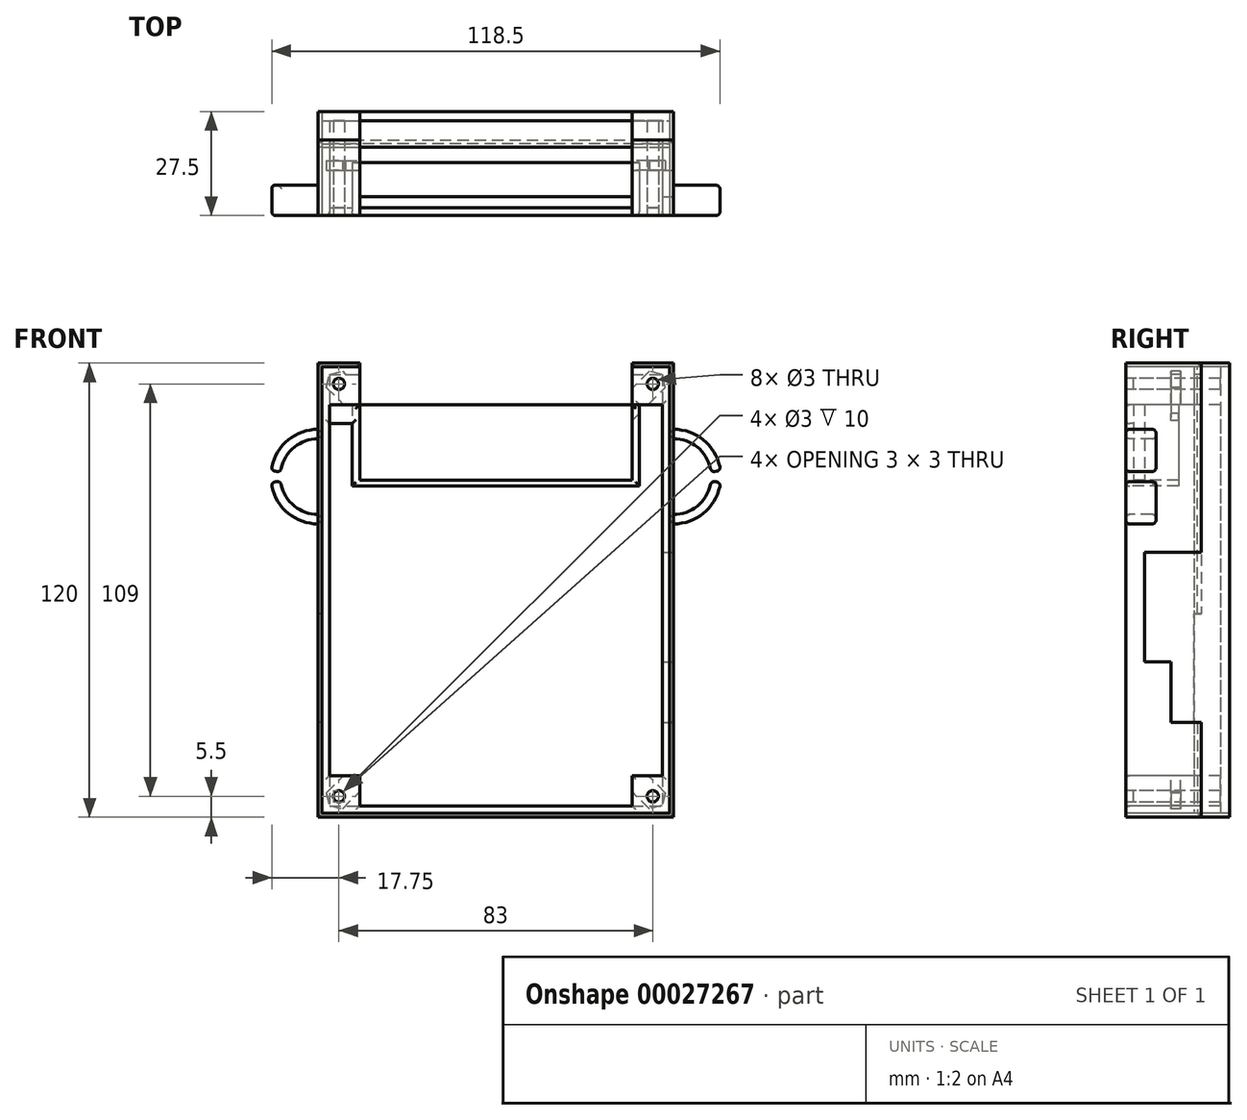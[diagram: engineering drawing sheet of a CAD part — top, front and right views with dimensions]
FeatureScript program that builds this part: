
annotation { "Feature Type Name" : "Feature", "Feature Type Description" : "" }
export const myFeature = defineFeature(function(context is Context, id is Id, definition is map)
    precondition{}
    {
        {
            var Q0;
            Q0=qCreatedBy(makeId("Front.planeOp"),FACE);
            var sketch = newSketch(context, id + "F0", { "sketchPlane" : qUnion([Q0])});
            skLineSegment(sketch, "E0.bottom", {"start": v(-41.5, 54.5) * mm, "end": v(41.5, 54.5) * mm, "construction": true});
            skLineSegment(sketch, "E1.left", {"start": v(-47, 60) * mm, "end": v(-47, -60) * mm});
            skLineSegment(sketch, "E0.top", {"start": v(-41.5, -54.5) * mm, "end": v(41.5, -54.5) * mm, "construction": true});
            skLineSegment(sketch, "E2.top", {"start": v(-46, -59) * mm, "end": v(46, -59) * mm});
            skLineSegment(sketch, "E0.left", {"start": v(-41.5, 54.5) * mm, "end": v(-41.5, -54.5) * mm, "construction": true});
            skLineSegment(sketch, "E2.left", {"start": v(-46, 59) * mm, "end": v(-46, -59) * mm});
            skLineSegment(sketch, "E2.right", {"start": v(46, 59) * mm, "end": v(46, -59) * mm});
            skLineSegment(sketch, "E3.left", {"start": v(-44, 57) * mm, "end": v(-44, -57) * mm});
            skLineSegment(sketch, "E0.right", {"start": v(41.5, 54.5) * mm, "end": v(41.5, -54.5) * mm, "construction": true});
            skLineSegment(sketch, "E2.bottom", {"start": v(-46, 59) * mm, "end": v(46, 59) * mm});
            skLineSegment(sketch, "E4", {"start": v(0, 57) * mm, "end": v(0, -57) * mm, "construction": true});
            skLineSegment(sketch, "E3.top", {"start": v(-44, -57) * mm, "end": v(44, -57) * mm});
            skLineSegment(sketch, "E5.right", {"start": v(36, -57) * mm, "end": v(36, -49) * mm});
            skLineSegment(sketch, "E6", {"start": v(-46, 0) * mm, "end": v(46, 0) * mm, "construction": true});
            skLineSegment(sketch, "E1.right", {"start": v(47, 60) * mm, "end": v(47, -60) * mm});
            skLineSegment(sketch, "E7.top", {"start": v(-44, -49) * mm, "end": v(-36, -49) * mm});
            skLineSegment(sketch, "E8.top", {"start": v(-44, 49) * mm, "end": v(-36, 49) * mm});
            skLineSegment(sketch, "E9.right", {"start": v(36, 57) * mm, "end": v(36, 49) * mm});
            skLineSegment(sketch, "E1.top", {"start": v(-47, -60) * mm, "end": v(47, -60) * mm});
            skLineSegment(sketch, "E7.right", {"start": v(-36, -57) * mm, "end": v(-36, -49) * mm});
            skLineSegment(sketch, "E5.top", {"start": v(44, -49) * mm, "end": v(36, -49) * mm});
            skLineSegment(sketch, "E3.right", {"start": v(44, 57) * mm, "end": v(44, -57) * mm});
            skPoint(sketch, "E10.rect.middle", {"position": v(0, 0) * mm});
            skLineSegment(sketch, "E8.right", {"start": v(-36, 57) * mm, "end": v(-36, 49) * mm});
            skLineSegment(sketch, "E3.bottom", {"start": v(-44, 57) * mm, "end": v(44, 57) * mm});
            skLineSegment(sketch, "E1.bottom", {"start": v(-47, 60) * mm, "end": v(47, 60) * mm});
            skLineSegment(sketch, "E9.top", {"start": v(44, 49) * mm, "end": v(36, 49) * mm});
            skLineSegment(sketch, "E7.bottom", {"start": v(-44, -57) * mm, "end": v(-36, -57) * mm});
            skLineSegment(sketch, "E7.left", {"start": v(-44, -57) * mm, "end": v(-44, -49) * mm});
            skLineSegment(sketch, "E11", {"start": v(0, 60) * mm, "end": v(0, -60) * mm, "construction": true});
            skLineSegment(sketch, "E12", {"start": v(0, 59) * mm, "end": v(0, -59) * mm, "construction": true});
            skLineSegment(sketch, "E5.bottom", {"start": v(44, -57) * mm, "end": v(36, -57) * mm});
            skLineSegment(sketch, "E13", {"start": v(-47, 0) * mm, "end": v(47, 0) * mm, "construction": true});
            skLineSegment(sketch, "E8.left", {"start": v(-44, 57) * mm, "end": v(-44, 49) * mm});
            skLineSegment(sketch, "E8.bottom", {"start": v(-44, 57) * mm, "end": v(-36, 57) * mm});
            skLineSegment(sketch, "E9.left", {"start": v(44, 57) * mm, "end": v(44, 49) * mm});
            skLineSegment(sketch, "E14", {"start": v(0, 54.5) * mm, "end": v(0, -54.5) * mm, "construction": true});
            skLineSegment(sketch, "E5.left", {"start": v(44, -57) * mm, "end": v(44, -49) * mm});
            skLineSegment(sketch, "E15", {"start": v(-44, 0) * mm, "end": v(44, 0) * mm, "construction": true});
            skLineSegment(sketch, "E9.bottom", {"start": v(44, 57) * mm, "end": v(36, 57) * mm});
            skLineSegment(sketch, "E16", {"start": v(-41.5, 0) * mm, "end": v(41.5, 0) * mm, "construction": true});
            skCircle(sketch, "E17", {"center": v(41.5, 54.5) * mm, "radius": 1.5 * mm});
            skCircle(sketch, "E18", {"center": v(-41.5, -54.5) * mm, "radius": 1.5 * mm});
            skCircle(sketch, "E19", {"center": v(41.5, -54.5) * mm, "radius": 1.5 * mm});
            skCircle(sketch, "E20", {"center": v(-41.5, 54.5) * mm, "radius": 1.5 * mm});
            skLineSegment(sketch, "E21.bottom", {"start": v(36, 60) * mm, "end": v(-36, 60) * mm});
            skLineSegment(sketch, "E21.top", {"start": v(36, 49) * mm, "end": v(-36, 49) * mm});
            skLineSegment(sketch, "E21.left", {"start": v(36, 60) * mm, "end": v(36, 49) * mm});
            skLineSegment(sketch, "E21.right", {"start": v(-36, 60) * mm, "end": v(-36, 49) * mm});
            skLineSegment(sketch, "E22.top", {"start": v(36, 29) * mm, "end": v(-36, 29) * mm});
            skLineSegment(sketch, "E22.left", {"start": v(36, 49) * mm, "end": v(36, 29) * mm});
            skLineSegment(sketch, "E22.right", {"start": v(-36, 49) * mm, "end": v(-36, 29) * mm});
            skLineSegment(sketch, "E23.bottom", {"start": v(38, 49) * mm, "end": v(-38, 49) * mm});
            skLineSegment(sketch, "E23.top", {"start": v(38, 27.5) * mm, "end": v(-38, 27.5) * mm});
            skLineSegment(sketch, "E23.left", {"start": v(38, 49) * mm, "end": v(38, 27.5) * mm});
            skLineSegment(sketch, "E23.right", {"start": v(-38, 49) * mm, "end": v(-38, 27.5) * mm});
            skLineSegment(sketch, "E24.bottom", {"start": v(-44, 49) * mm, "end": v(-38, 49) * mm});
            skLineSegment(sketch, "E24.top", {"start": v(-44, 44) * mm, "end": v(-38, 44) * mm});
            skLineSegment(sketch, "E24.left", {"start": v(-44, 49) * mm, "end": v(-44, 44) * mm});
            skLineSegment(sketch, "E24.right", {"start": v(-38, 49) * mm, "end": v(-38, 44) * mm});
            skLineSegment(sketch, "E25.bottom", {"start": v(44, 49) * mm, "end": v(38, 49) * mm});
            skLineSegment(sketch, "E25.top", {"start": v(44, 44) * mm, "end": v(38, 44) * mm});
            skLineSegment(sketch, "E25.left", {"start": v(44, 49) * mm, "end": v(44, 44) * mm});
            skLineSegment(sketch, "E25.right", {"start": v(38, 49) * mm, "end": v(38, 44) * mm});
            skSolve(sketch);
        }
        {
            var Q0;
            Q0=makeQuery(id+"F0.imprint","IMPRINT",FACE,{"disambiguationData":[TD([[makeQuery(id+"F0.imprint","IMPRINT",EDGE,{"derivedFrom":sQuery(id+"F0.wireOp",EDGE,"E3.left")}),1.0]])]});
            var Q1;
            Q1=makeQuery(id+"F0.imprint","IMPRINT",FACE,{"disambiguationData":[TD([[makeQuery(id+"F0.imprint","IMPRINT",EDGE,{"derivedFrom":sQuery(id+"F0.wireOp",EDGE,"E2.top")}),1.0]])]});
            var Q2;
            {var subQ1=sQuery(id+"F0.wireOp",EDGE,"E9.top");Q2=makeQuery(id+"F0.imprint","IMPRINT",FACE,{"disambiguationData":[TD([[makeQuery(id+"F0.imprint","IMPRINT",EDGE,{"derivedFrom":subQ1}),-1.0]])]});}
            var Q3;
            Q3=makeQuery(id+"F0.imprint","IMPRINT",FACE,{"disambiguationData":[TD([[makeQuery(id+"F0.imprint","IMPRINT",EDGE,{"derivedFrom":sQuery(id+"F0.wireOp",EDGE,"E5.right")}),-1.0]])]});
            var Q4;
            Q4=makeQuery(id+"F0.imprint","IMPRINT",FACE,{"disambiguationData":[TD([[makeQuery(id+"F0.imprint","IMPRINT",EDGE,{"derivedFrom":sQuery(id+"F0.wireOp",EDGE,"E21.top")}),1.0]])]});
            var Q5;
            {var subQ8=sQuery(id+"F0.wireOp",EDGE,"E1.left");Q5=makeQuery(id+"F0.imprint","IMPRINT",FACE,{"disambiguationData":[TD([[makeQuery(id+"F0.imprint","IMPRINT",EDGE,{"derivedFrom":subQ8}),1.0]])]});}
            var Q6;
            Q6=makeQuery(id+"F0.imprint","IMPRINT",FACE,{"disambiguationData":[TD([[makeQuery(id+"F0.imprint","IMPRINT",EDGE,{"derivedFrom":sQuery(id+"F0.wireOp",EDGE,"E7.top")}),-1.0]])]});
            var Q7;
            Q7=makeQuery(id+"F0.imprint","IMPRINT",FACE,{"disambiguationData":[TD([[makeQuery(id+"F0.imprint","IMPRINT",EDGE,{"derivedFrom":sQuery(id+"F0.wireOp",EDGE,"E17")}),1.0]])]});
            var Q8;
            {var subQ0=sQuery(id+"F0.wireOp",EDGE,"E8.top");Q8=makeQuery(id+"F0.imprint","IMPRINT",FACE,{"disambiguationData":[TD([[makeQuery(id+"F0.imprint","IMPRINT",EDGE,{"derivedFrom":subQ0}),1.0]])]});}
            var Q9;
            Q9=makeQuery(id+"F0.imprint","IMPRINT",FACE,{"disambiguationData":[TD([[makeQuery(id+"F0.imprint","IMPRINT",EDGE,{"derivedFrom":sQuery(id+"F0.wireOp",EDGE,"E19")}),1.0]])]});
            var Q10;
            Q10=makeQuery(id+"F0.imprint","IMPRINT",FACE,{"disambiguationData":[TD([[makeQuery(id+"F0.imprint","IMPRINT",EDGE,{"derivedFrom":sQuery(id+"F0.wireOp",EDGE,"E20")}),1.0]])]});
            var Q11;
            Q11=makeQuery(id+"F0.imprint","IMPRINT",FACE,{"disambiguationData":[TD([[makeQuery(id+"F0.imprint","IMPRINT",EDGE,{"derivedFrom":sQuery(id+"F0.wireOp",EDGE,"E18")}),1.0]])]});
            var Q12;
            Q12=makeQuery(id+"F0.imprint","IMPRINT",FACE,{"disambiguationData":[TD([[makeQuery(id+"F0.imprint","IMPRINT",EDGE,{"derivedFrom":sQuery(id+"F0.wireOp",EDGE,"E22.top")}),1.0]])]});
            var Q13;
            Q13=makeQuery(id+"F0.imprint","IMPRINT",FACE,{"disambiguationData":[TD([[makeQuery(id+"F0.imprint","IMPRINT",EDGE,{"derivedFrom":sQuery(id+"F0.wireOp",EDGE,"E25.bottom")}),1.0]])]});
            var Q14;
            Q14=makeQuery(id+"F0.imprint","IMPRINT",FACE,{"disambiguationData":[TD([[makeQuery(id+"F0.imprint","IMPRINT",EDGE,{"derivedFrom":sQuery(id+"F0.wireOp",EDGE,"E24.bottom")}),-1.0]])]});
            var Q15;
            Q15=makeQuery(id+"F0.imprint","IMPRINT",FACE,{"disambiguationData":[TD([[makeQuery(id+"F0.imprint","IMPRINT",EDGE,{"derivedFrom":sQuery(id+"F0.wireOp",EDGE,"E8.left")}),1.0]])]});
            var Q16;
            Q16=makeQuery(id+"F0.imprint","IMPRINT",FACE,{"disambiguationData":[TD([[makeQuery(id+"F0.imprint","IMPRINT",EDGE,{"derivedFrom":sQuery(id+"F0.wireOp",EDGE,"E9.left")}),-1.0]])]});
            extrude(context, id + "F1", {"entities" : qUnion([Q0, Q1, Q2, Q3, Q4, Q5, Q6, Q7, Q8, Q9, Q10, Q11, Q12, Q13, Q14, Q15, Q16]), "oppositeDirection" : true, "depth" : 2 * mm});
        }
        {
            var Q0;
            Q0=makeQuery(id+"F0.imprint","IMPRINT",FACE,{"disambiguationData":[TD([[makeQuery(id+"F0.imprint","IMPRINT",EDGE,{"derivedFrom":sQuery(id+"F0.wireOp",EDGE,"E2.top")}),1.0]])]});
            extrude(context, id + "F2", {"entities" : qUnion([Q0]), "operationType" : NewBodyOperationType.ADD, "oppositeDirection" : true, "depth" : 18 * mm});
        }
        {
            var Q0;
            {var subQ8=sQuery(id+"F0.wireOp",EDGE,"E1.left");Q0=makeQuery(id+"F0.imprint","IMPRINT",FACE,{"disambiguationData":[TD([[makeQuery(id+"F0.imprint","IMPRINT",EDGE,{"derivedFrom":subQ8}),1.0]])]});}
            var Q1;
            Q1=makeQuery(id+"F0.imprint","IMPRINT",FACE,{"disambiguationData":[TD([[makeQuery(id+"F0.imprint","IMPRINT",EDGE,{"derivedFrom":sQuery(id+"F0.wireOp",EDGE,"E7.top")}),-1.0]])]});
            var Q2;
            {var subQ0=sQuery(id+"F0.wireOp",EDGE,"E8.top");Q2=makeQuery(id+"F0.imprint","IMPRINT",FACE,{"disambiguationData":[TD([[makeQuery(id+"F0.imprint","IMPRINT",EDGE,{"derivedFrom":subQ0}),1.0]])]});}
            var Q3;
            {var subQ1=sQuery(id+"F0.wireOp",EDGE,"E9.top");Q3=makeQuery(id+"F0.imprint","IMPRINT",FACE,{"disambiguationData":[TD([[makeQuery(id+"F0.imprint","IMPRINT",EDGE,{"derivedFrom":subQ1}),-1.0]])]});}
            var Q4;
            Q4=makeQuery(id+"F0.imprint","IMPRINT",FACE,{"disambiguationData":[TD([[makeQuery(id+"F0.imprint","IMPRINT",EDGE,{"derivedFrom":sQuery(id+"F0.wireOp",EDGE,"E8.left")}),1.0]])]});
            var Q5;
            Q5=makeQuery(id+"F0.imprint","IMPRINT",FACE,{"disambiguationData":[TD([[makeQuery(id+"F0.imprint","IMPRINT",EDGE,{"derivedFrom":sQuery(id+"F0.wireOp",EDGE,"E24.bottom")}),-1.0]])]});
            var Q6;
            Q6=makeQuery(id+"F0.imprint","IMPRINT",FACE,{"disambiguationData":[TD([[makeQuery(id+"F0.imprint","IMPRINT",EDGE,{"derivedFrom":sQuery(id+"F0.wireOp",EDGE,"E9.left")}),-1.0]])]});
            var Q7;
            Q7=makeQuery(id+"F0.imprint","IMPRINT",FACE,{"disambiguationData":[TD([[makeQuery(id+"F0.imprint","IMPRINT",EDGE,{"derivedFrom":sQuery(id+"F0.wireOp",EDGE,"E5.right")}),-1.0]])]});
            var Q8;
            Q8=makeQuery(id+"F0.imprint","IMPRINT",FACE,{"disambiguationData":[TD([[makeQuery(id+"F0.imprint","IMPRINT",EDGE,{"derivedFrom":sQuery(id+"F0.wireOp",EDGE,"E25.bottom")}),1.0]])]});
            extrude(context, id + "F3", {"entities" : qUnion([Q0, Q1, Q2, Q3, Q4, Q5, Q6, Q7, Q8]), "operationType" : NewBodyOperationType.ADD, "oppositeDirection" : true, "depth" : 20 * mm});
        }
        {
            var Q0;
            Q0=makeQuery(id+"F0.imprint","IMPRINT",FACE,{"disambiguationData":[TD([[makeQuery(id+"F0.imprint","IMPRINT",EDGE,{"derivedFrom":sQuery(id+"F0.wireOp",EDGE,"E22.top")}),1.0]])]});
            extrude(context, id + "F4", {"entities" : qUnion([Q0]), "operationType" : NewBodyOperationType.ADD, "oppositeDirection" : true, "depth" : 14 * mm});
        }
        {
            var Q0;
            {var subQ0=sQuery(id+"F0.wireOp",EDGE,"E1.left");Q0=makeQuery(id+"F3.boolean.opBoolean","MERGE",FACE,{"derivedFrom":[makeQuery(id+"F1.opExtrude","SWEPT_FACE",FACE,{"disambiguationData":[OSD([subQ0])]}),makeQuery(id+"F3.opExtrude","SWEPT_FACE",FACE,{"disambiguationData":[OSD([subQ0])]})]});}
            var sketch = newSketch(context, id + "F5", { "sketchPlane" : qUnion([Q0])});
            skLineSegment(sketch, "E26.bottom", {"start": v(-20, -35) * mm, "end": v(-18, -35) * mm});
            skLineSegment(sketch, "E26.top", {"start": v(-20, -6.2) * mm, "end": v(-18, -6.2) * mm});
            skLineSegment(sketch, "E26.left", {"start": v(-20, -35) * mm, "end": v(-20, -6.2) * mm});
            skLineSegment(sketch, "E26.right", {"start": v(-18, -35) * mm, "end": v(-18, -6.2) * mm});
            skSolve(sketch);
        }
        {
            var Q0;
            {var subQ0=sQuery(id+"F0.wireOp",EDGE,"E1.right");Q0=makeQuery(id+"F3.boolean.opBoolean","MERGE",FACE,{"derivedFrom":[makeQuery(id+"F1.opExtrude","SWEPT_FACE",FACE,{"disambiguationData":[OSD([subQ0])]}),makeQuery(id+"F3.opExtrude","SWEPT_FACE",FACE,{"disambiguationData":[OSD([subQ0])]})]});}
            var sketch = newSketch(context, id + "F6", { "sketchPlane" : qUnion([Q0])});
            skLineSegment(sketch, "E27.bottom", {"start": v(20, -35) * mm, "end": v(12, -35) * mm});
            skLineSegment(sketch, "E27.top", {"start": v(20, -19) * mm, "end": v(12, -19) * mm});
            skLineSegment(sketch, "E27.left", {"start": v(20, -35) * mm, "end": v(20, -19) * mm});
            skLineSegment(sketch, "E27.right", {"start": v(12, -35) * mm, "end": v(12, -19) * mm});
            skLineSegment(sketch, "E28.bottom", {"start": v(20, -19) * mm, "end": v(5, -19) * mm});
            skLineSegment(sketch, "E28.top", {"start": v(20, 10) * mm, "end": v(5, 10) * mm});
            skLineSegment(sketch, "E28.left", {"start": v(20, -19) * mm, "end": v(20, 10) * mm});
            skLineSegment(sketch, "E28.right", {"start": v(5, -19) * mm, "end": v(5, 10) * mm});
            skSolve(sketch);
        }
        {
            var Q0;
            Q0=makeQuery(id+"F5.imprint","IMPRINT",FACE,{"disambiguationData":[TD([[makeQuery(id+"F5.imprint","IMPRINT",EDGE,{"derivedFrom":sQuery(id+"F5.wireOp",EDGE,"E26.bottom")}),1.0]])]});
            extrude(context, id + "F7", {"entities" : qUnion([Q0]), "operationType" : NewBodyOperationType.REMOVE, "endBound" : BoundingType.UP_TO_NEXT, "oppositeDirection" : true, "depth" : 25 * mm});
        }
        {
            var Q0;
            Q0=makeQuery(id+"F6.imprint","IMPRINT",FACE,{"disambiguationData":[TD([[makeQuery(id+"F6.imprint","IMPRINT",EDGE,{"derivedFrom":sQuery(id+"F6.wireOp",EDGE,"E27.bottom")}),-1.0]])]});
            var Q1;
            Q1=makeQuery(id+"F6.imprint","IMPRINT",FACE,{"disambiguationData":[TD([[makeQuery(id+"F6.imprint","IMPRINT",EDGE,{"derivedFrom":sQuery(id+"F6.wireOp",EDGE,"E28.top")}),1.0]])]});
            extrude(context, id + "F8", {"entities" : qUnion([Q0, Q1]), "operationType" : NewBodyOperationType.REMOVE, "endBound" : BoundingType.UP_TO_NEXT, "oppositeDirection" : true, "depth" : 25 * mm});
        }
        {
            var Q0;
            Q0=makeQuery(id+"F8.boolean.opBoolean","COPY",FACE,{"derivedFrom":makeQuery(id+"F8.opExtrude","SWEPT_FACE",FACE,{"disambiguationData":[OSD([sQuery(id+"F6.wireOp",EDGE,"E27.right")])]})});
            var sketch = newSketch(context, id + "F9", { "sketchPlane" : qUnion([Q0])});
            skLineSegment(sketch, "E29.0", {"start": v(-36, -57) * mm, "end": v(-36, -49) * mm});
            skCircle(sketch, "E29.1", {"center": v(-41.5, -54.5) * mm, "radius": 1.5 * mm});
            skLineSegment(sketch, "E29.2", {"start": v(-44, -57) * mm, "end": v(-36, -57) * mm});
            skLineSegment(sketch, "E29.3", {"start": v(-44, -57) * mm, "end": v(-44, -49) * mm});
            skLineSegment(sketch, "E29.4", {"start": v(-44, -49) * mm, "end": v(-36, -49) * mm});
            skLineSegment(sketch, "E30", {"start": v(-42.4, -51.15) * mm, "end": v(-44.85, -53.6) * mm});
            skLineSegment(sketch, "E31", {"start": v(-44.85, -53.6) * mm, "end": v(-43.95, -56.95) * mm});
            skLineSegment(sketch, "E32", {"start": v(-43.95, -56.95) * mm, "end": v(-40.6, -57.85) * mm});
            skLineSegment(sketch, "E33", {"start": v(-40.6, -57.85) * mm, "end": v(-38.15, -55.4) * mm});
            skLineSegment(sketch, "E34", {"start": v(-38.15, -55.4) * mm, "end": v(-39.05, -52.05) * mm});
            skLineSegment(sketch, "E35", {"start": v(-39.05, -52.05) * mm, "end": v(-42.4, -51.15) * mm});
            skLineSegment(sketch, "E36", {"start": v(-42.4, -51.15) * mm, "end": v(-40.6, -57.85) * mm, "construction": true});
            skLineSegment(sketch, "E37", {"start": v(-44.85, -53.6) * mm, "end": v(-38.15, -55.4) * mm, "construction": true});
            skLineSegment(sketch, "E38", {"start": v(-43.95, -56.95) * mm, "end": v(-39.05, -52.05) * mm, "construction": true});
            skLineSegment(sketch, "E39", {"start": v(-44, -57) * mm, "end": v(-36, -49) * mm, "construction": true});
            skLineSegment(sketch, "E40", {"start": v(-38.15, -55.4) * mm, "end": v(-36, -53.24) * mm});
            skLineSegment(sketch, "E41", {"start": v(-36, -53.24) * mm, "end": v(-36, -49) * mm});
            skLineSegment(sketch, "E42", {"start": v(-42.4, -51.15) * mm, "end": v(-40.24, -49) * mm});
            skLineSegment(sketch, "E43", {"start": v(-40.24, -49) * mm, "end": v(-36, -49) * mm});
            skLineSegment(sketch, "E44.MirrorCS", {"start": v(40.24, -49) * mm, "end": v(36, -49) * mm});
            skLineSegment(sketch, "E45.MirrorCS", {"start": v(36, -53.24) * mm, "end": v(36, -49) * mm});
            skLineSegment(sketch, "E46.MirrorCS", {"start": v(43.95, -56.95) * mm, "end": v(39.05, -52.05) * mm});
            skLineSegment(sketch, "E47.MirrorCS", {"start": v(44.85, -53.6) * mm, "end": v(38.15, -55.4) * mm});
            skLineSegment(sketch, "E48.MirrorCS", {"start": v(42.4, -51.15) * mm, "end": v(40.6, -57.85) * mm});
            skLineSegment(sketch, "E49.MirrorCS", {"start": v(44, -57) * mm, "end": v(36, -49) * mm});
            skLineSegment(sketch, "E50.MirrorCS", {"start": v(43.95, -56.95) * mm, "end": v(40.6, -57.85) * mm});
            skPoint(sketch, "E51.MirrorP", {"position": v(41.5, -54.5) * mm});
            skLineSegment(sketch, "E52.MirrorCS", {"start": v(44, -57) * mm, "end": v(44, -49) * mm});
            skLineSegment(sketch, "E53.MirrorCS", {"start": v(39.05, -52.05) * mm, "end": v(42.4, -51.15) * mm});
            skLineSegment(sketch, "E54.MirrorCS", {"start": v(44, -49) * mm, "end": v(36, -49) * mm});
            skLineSegment(sketch, "E55.MirrorCS", {"start": v(42.4, -51.15) * mm, "end": v(40.24, -49) * mm});
            skLineSegment(sketch, "E56.MirrorCS", {"start": v(36, -57) * mm, "end": v(36, -49) * mm});
            skLineSegment(sketch, "E57.MirrorCS", {"start": v(40.6, -57.85) * mm, "end": v(38.15, -55.4) * mm});
            skLineSegment(sketch, "E58.MirrorCS", {"start": v(44, -57) * mm, "end": v(36, -57) * mm});
            skLineSegment(sketch, "E59.MirrorCS", {"start": v(38.15, -55.4) * mm, "end": v(36, -53.24) * mm});
            skCircle(sketch, "E60.MirrorC", {"center": v(41.5, -54.5) * mm, "radius": 1.5 * mm});
            skLineSegment(sketch, "E61.MirrorCS", {"start": v(38.15, -55.4) * mm, "end": v(39.05, -52.05) * mm});
            skLineSegment(sketch, "E62.MirrorCS", {"start": v(42.4, -51.15) * mm, "end": v(44.85, -53.6) * mm});
            skLineSegment(sketch, "E63.MirrorCS", {"start": v(44.85, -53.6) * mm, "end": v(43.95, -56.95) * mm});
            skLineSegment(sketch, "E64.MirrorCS", {"start": v(-43.95, 56.95) * mm, "end": v(-39.05, 52.05) * mm});
            skLineSegment(sketch, "E65.MirrorCS", {"start": v(-38.15, 55.4) * mm, "end": v(-36, 53.24) * mm});
            skLineSegment(sketch, "E66.MirrorCS", {"start": v(43.95, 56.95) * mm, "end": v(39.05, 52.05) * mm});
            skLineSegment(sketch, "E67.MirrorCS", {"start": v(40.24, 49) * mm, "end": v(36, 49) * mm});
            skLineSegment(sketch, "E68.MirrorCS", {"start": v(-38.15, 55.4) * mm, "end": v(-39.05, 52.05) * mm});
            skLineSegment(sketch, "E69.MirrorCS", {"start": v(36, 53.24) * mm, "end": v(36, 49) * mm});
            skLineSegment(sketch, "E70.MirrorCS", {"start": v(-36, 53.24) * mm, "end": v(-36, 49) * mm});
            skLineSegment(sketch, "E71.MirrorCS", {"start": v(-44, 57) * mm, "end": v(-36, 49) * mm});
            skLineSegment(sketch, "E72.MirrorCS", {"start": v(38.15, 55.4) * mm, "end": v(39.05, 52.05) * mm});
            skLineSegment(sketch, "E73.MirrorCS", {"start": v(-40.6, 57.85) * mm, "end": v(-38.15, 55.4) * mm});
            skLineSegment(sketch, "E74.MirrorCS", {"start": v(-39.05, 52.05) * mm, "end": v(-42.4, 51.15) * mm});
            skLineSegment(sketch, "E75.MirrorCS", {"start": v(-44.85, 53.6) * mm, "end": v(-38.15, 55.4) * mm});
            skLineSegment(sketch, "E76.MirrorCS", {"start": v(-42.4, 51.15) * mm, "end": v(-40.6, 57.85) * mm});
            skLineSegment(sketch, "E77.MirrorCS", {"start": v(-44.85, 53.6) * mm, "end": v(-43.95, 56.95) * mm});
            skLineSegment(sketch, "E78.MirrorCS", {"start": v(-42.4, 51.15) * mm, "end": v(-44.85, 53.6) * mm});
            skLineSegment(sketch, "E79.MirrorCS", {"start": v(43.95, 56.95) * mm, "end": v(40.6, 57.85) * mm});
            skLineSegment(sketch, "E80.MirrorCS", {"start": v(-44, 57) * mm, "end": v(-44, 49) * mm});
            skLineSegment(sketch, "E81.MirrorCS", {"start": v(38.15, 55.4) * mm, "end": v(36, 53.24) * mm});
            skLineSegment(sketch, "E82.MirrorCS", {"start": v(-43.95, 56.95) * mm, "end": v(-40.6, 57.85) * mm});
            skLineSegment(sketch, "E83.MirrorCS", {"start": v(40.6, 57.85) * mm, "end": v(38.15, 55.4) * mm});
            skLineSegment(sketch, "E84.MirrorCS", {"start": v(44, 57) * mm, "end": v(36, 49) * mm});
            skLineSegment(sketch, "E85.MirrorCS", {"start": v(42.4, 51.15) * mm, "end": v(44.85, 53.6) * mm});
            skLineSegment(sketch, "E86.MirrorCS", {"start": v(42.4, 51.15) * mm, "end": v(40.6, 57.85) * mm});
            skLineSegment(sketch, "E87.MirrorCS", {"start": v(42.4, 51.15) * mm, "end": v(40.24, 49) * mm});
            skLineSegment(sketch, "E88.MirrorCS", {"start": v(39.05, 52.05) * mm, "end": v(42.4, 51.15) * mm});
            skLineSegment(sketch, "E89.MirrorCS", {"start": v(44.85, 53.6) * mm, "end": v(43.95, 56.95) * mm});
            skCircle(sketch, "E90.MirrorC", {"center": v(-41.5, 54.5) * mm, "radius": 1.5 * mm});
            skLineSegment(sketch, "E91.MirrorCS", {"start": v(-36, 57) * mm, "end": v(-36, 49) * mm});
            skLineSegment(sketch, "E92.MirrorCS", {"start": v(44, 57) * mm, "end": v(36, 57) * mm});
            skLineSegment(sketch, "E93.MirrorCS", {"start": v(44.85, 53.6) * mm, "end": v(38.15, 55.4) * mm});
            skLineSegment(sketch, "E94.MirrorCS", {"start": v(-40.24, 49) * mm, "end": v(-36, 49) * mm});
            skCircle(sketch, "E95.MirrorC", {"center": v(41.5, 54.5) * mm, "radius": 1.5 * mm});
            skLineSegment(sketch, "E96.MirrorCS", {"start": v(-42.4, 51.15) * mm, "end": v(-40.24, 49) * mm});
            skLineSegment(sketch, "E97.MirrorCS", {"start": v(36, 57) * mm, "end": v(36, 49) * mm});
            skLineSegment(sketch, "E98.MirrorCS", {"start": v(44, 49) * mm, "end": v(36, 49) * mm});
            skLineSegment(sketch, "E99.MirrorCS", {"start": v(-44, 49) * mm, "end": v(-36, 49) * mm});
            skLineSegment(sketch, "E100.MirrorCS", {"start": v(44, 57) * mm, "end": v(44, 49) * mm});
            skLineSegment(sketch, "E101.MirrorCS", {"start": v(-44, 57) * mm, "end": v(-36, 57) * mm});
            skLineSegment(sketch, "E102.0", {"start": v(-36, 49) * mm, "end": v(-36, 29) * mm});
            skLineSegment(sketch, "E103.1", {"start": v(36, 49) * mm, "end": v(36, 29) * mm});
            skLineSegment(sketch, "E104", {"start": v(40.24, 49) * mm, "end": v(36, 44.76) * mm});
            skLineSegment(sketch, "E105", {"start": v(-40.24, 49) * mm, "end": v(-36, 44.76) * mm});
            skSolve(sketch);
        }
        {
            var Q0;
            {var subQ4=sQuery(id+"F9.wireOp",EDGE,"E53.MirrorCS");Q0=makeQuery(id+"F9.imprint","IMPRINT",FACE,{"disambiguationData":[TD([[makeQuery(id+"F9.imprint","IMPRINT",EDGE,{"derivedFrom":subQ4}),1.0]])]});}
            var Q1;
            {var subQ1=sQuery(id+"F9.wireOp",EDGE,"E59.MirrorCS");Q1=makeQuery(id+"F9.imprint","IMPRINT",FACE,{"disambiguationData":[TD([[makeQuery(id+"F9.imprint","IMPRINT",EDGE,{"derivedFrom":subQ1}),-1.0]])]});}
            var Q2;
            {var subQ0=sQuery(id+"F9.wireOp",EDGE,"E61.MirrorCS");Q2=makeQuery(id+"F9.imprint","IMPRINT",FACE,{"disambiguationData":[TD([[makeQuery(id+"F9.imprint","IMPRINT",EDGE,{"derivedFrom":subQ0}),-1.0]])]});}
            var Q3;
            {var subQ0=sQuery(id+"F9.wireOp",EDGE,"E48.MirrorCS");var subQ3=sQuery(id+"F9.wireOp",EDGE,"E60.MirrorC");var subQ4=makeQuery(id+"F9.imprint","INTERSECT",VERTEX,{"disambiguationData":[OD(1.0)],"derivedFrom":[subQ0,subQ3]});Q3=makeQuery(id+"F9.imprint","IMPRINT",FACE,{"disambiguationData":[TD([[makeQuery(id+"F9.imprint","IMPRINT",EDGE,{"disambiguationData":[TD([[subQ4,-1.0]])],"derivedFrom":subQ0}),-1.0]])]});}
            var Q4;
            {var subQ0=sQuery(id+"F9.wireOp",EDGE,"E48.MirrorCS");var subQ3=sQuery(id+"F9.wireOp",EDGE,"E60.MirrorC");var subQ4=makeQuery(id+"F9.imprint","INTERSECT",VERTEX,{"disambiguationData":[OD(1.0)],"derivedFrom":[subQ0,subQ3]});Q4=makeQuery(id+"F9.imprint","IMPRINT",FACE,{"disambiguationData":[TD([[makeQuery(id+"F9.imprint","IMPRINT",EDGE,{"disambiguationData":[TD([[subQ4,-1.0]])],"derivedFrom":subQ0}),1.0]])]});}
            var Q5;
            {var subQ0=sQuery(id+"F9.wireOp",EDGE,"E58.MirrorCS");var subQ3=sQuery(id+"F9.wireOp",EDGE,"E50.MirrorCS");var subQ4=makeQuery(id+"F9.imprint","INTERSECT",VERTEX,{"derivedFrom":[subQ3,subQ0]});Q5=makeQuery(id+"F9.imprint","IMPRINT",FACE,{"disambiguationData":[TD([[makeQuery(id+"F9.imprint","IMPRINT",EDGE,{"disambiguationData":[TD([[subQ4,-1.0]])],"derivedFrom":subQ0}),1.0]])]});}
            var Q6;
            {var subQ0=sQuery(id+"F9.wireOp",EDGE,"E58.MirrorCS");var subQ3=sQuery(id+"F9.wireOp",EDGE,"E57.MirrorCS");var subQ4=makeQuery(id+"F9.imprint","INTERSECT",VERTEX,{"derivedFrom":[subQ3,subQ0]});Q6=makeQuery(id+"F9.imprint","IMPRINT",FACE,{"disambiguationData":[TD([[makeQuery(id+"F9.imprint","IMPRINT",EDGE,{"disambiguationData":[TD([[subQ4,1.0]])],"derivedFrom":subQ0}),1.0]])]});}
            var Q7;
            {var subQ0=sQuery(id+"F9.wireOp",EDGE,"E53.MirrorCS");Q7=makeQuery(id+"F9.imprint","IMPRINT",FACE,{"disambiguationData":[TD([[makeQuery(id+"F9.imprint","IMPRINT",EDGE,{"derivedFrom":subQ0}),-1.0]])]});}
            var Q8;
            {var subQ1=sQuery(id+"F9.wireOp",EDGE,"E52.MirrorCS");var subQ5=sQuery(id+"F9.wireOp",EDGE,"E47.MirrorCS");var subQ8=makeQuery(id+"F9.imprint","INTERSECT",VERTEX,{"derivedFrom":[subQ5,subQ1]});Q8=makeQuery(id+"F9.imprint","IMPRINT",FACE,{"disambiguationData":[TD([[makeQuery(id+"F9.imprint","IMPRINT",EDGE,{"disambiguationData":[TD([[subQ8,-1.0]])],"derivedFrom":subQ5}),-1.0]])]});}
            var Q9;
            {var subQ1=sQuery(id+"F9.wireOp",EDGE,"E52.MirrorCS");var subQ5=sQuery(id+"F9.wireOp",EDGE,"E47.MirrorCS");var subQ6=makeQuery(id+"F9.imprint","INTERSECT",VERTEX,{"derivedFrom":[subQ5,subQ1]});Q9=makeQuery(id+"F9.imprint","IMPRINT",FACE,{"disambiguationData":[TD([[makeQuery(id+"F9.imprint","IMPRINT",EDGE,{"disambiguationData":[TD([[subQ6,-1.0]])],"derivedFrom":subQ5}),1.0]])]});}
            var Q10;
            {var subQ0=sQuery(id+"F9.wireOp",EDGE,"E63.MirrorCS");var subQ1=sQuery(id+"F9.wireOp",EDGE,"E52.MirrorCS");var subQ2=makeQuery(id+"F9.imprint","INTERSECT",VERTEX,{"derivedFrom":[subQ1,subQ0]});Q10=makeQuery(id+"F9.imprint","IMPRINT",FACE,{"disambiguationData":[TD([[makeQuery(id+"F9.imprint","IMPRINT",EDGE,{"disambiguationData":[TD([[subQ2,-1.0]])],"derivedFrom":subQ1}),-1.0]])]});}
            var Q11;
            {var subQ0=sQuery(id+"F9.wireOp",EDGE,"E62.MirrorCS");var subQ1=sQuery(id+"F9.wireOp",EDGE,"E52.MirrorCS");var subQ2=makeQuery(id+"F9.imprint","INTERSECT",VERTEX,{"derivedFrom":[subQ1,subQ0]});Q11=makeQuery(id+"F9.imprint","IMPRINT",FACE,{"disambiguationData":[TD([[makeQuery(id+"F9.imprint","IMPRINT",EDGE,{"disambiguationData":[TD([[subQ2,1.0]])],"derivedFrom":subQ1}),-1.0]])]});}
            var Q12;
            Q12=makeQuery(id+"F9.imprint","IMPRINT",FACE,{"disambiguationData":[TD([[makeQuery(id+"F9.imprint","IMPRINT",EDGE,{"derivedFrom":sQuery(id+"F9.wireOp",EDGE,"E34")}),-1.0]])]});
            var Q13;
            Q13=makeQuery(id+"F9.imprint","IMPRINT",FACE,{"disambiguationData":[TD([[makeQuery(id+"F9.imprint","IMPRINT",EDGE,{"derivedFrom":sQuery(id+"F9.wireOp",EDGE,"E29.1")}),-1.0]])]});
            var Q14;
            {var subQ1=sQuery(id+"F9.wireOp",EDGE,"E29.2");var subQ3=sQuery(id+"F9.wireOp",EDGE,"E32");var subQ5=makeQuery(id+"F9.imprint","INTERSECT",VERTEX,{"derivedFrom":[subQ1,subQ3]});Q14=makeQuery(id+"F9.imprint","IMPRINT",FACE,{"disambiguationData":[TD([[makeQuery(id+"F9.imprint","IMPRINT",EDGE,{"disambiguationData":[TD([[subQ5,-1.0]])],"derivedFrom":subQ1}),-1.0]])]});}
            var Q15;
            {var subQ0=sQuery(id+"F9.wireOp",EDGE,"E31");var subQ1=sQuery(id+"F9.wireOp",EDGE,"E29.3");var subQ2=makeQuery(id+"F9.imprint","INTERSECT",VERTEX,{"derivedFrom":[subQ1,subQ0]});Q15=makeQuery(id+"F9.imprint","IMPRINT",FACE,{"disambiguationData":[TD([[makeQuery(id+"F9.imprint","IMPRINT",EDGE,{"disambiguationData":[TD([[subQ2,-1.0]])],"derivedFrom":subQ1}),1.0]])]});}
            var Q16;
            {var subQ1=sQuery(id+"F9.wireOp",EDGE,"E76.MirrorCS");var subQ7=sQuery(id+"F9.wireOp",EDGE,"E90.MirrorC");var subQ9=makeQuery(id+"F9.imprint","INTERSECT",VERTEX,{"disambiguationData":[OD(1.0)],"derivedFrom":[subQ1,subQ7]});Q16=makeQuery(id+"F9.imprint","IMPRINT",FACE,{"disambiguationData":[TD([[makeQuery(id+"F9.imprint","IMPRINT",EDGE,{"disambiguationData":[TD([[subQ9,-1.0]])],"derivedFrom":subQ1}),-1.0]])]});}
            var Q17;
            {var subQ1=sQuery(id+"F9.wireOp",EDGE,"E76.MirrorCS");var subQ6=sQuery(id+"F9.wireOp",EDGE,"E90.MirrorC");var subQ9=makeQuery(id+"F9.imprint","INTERSECT",VERTEX,{"disambiguationData":[OD(1.0)],"derivedFrom":[subQ1,subQ6]});Q17=makeQuery(id+"F9.imprint","IMPRINT",FACE,{"disambiguationData":[TD([[makeQuery(id+"F9.imprint","IMPRINT",EDGE,{"disambiguationData":[TD([[subQ9,-1.0]])],"derivedFrom":subQ1}),1.0]])]});}
            var Q18;
            {var subQ0=sQuery(id+"F9.wireOp",EDGE,"E101.MirrorCS");var subQ3=sQuery(id+"F9.wireOp",EDGE,"E82.MirrorCS");var subQ4=makeQuery(id+"F9.imprint","INTERSECT",VERTEX,{"derivedFrom":[subQ3,subQ0]});Q18=makeQuery(id+"F9.imprint","IMPRINT",FACE,{"disambiguationData":[TD([[makeQuery(id+"F9.imprint","IMPRINT",EDGE,{"disambiguationData":[TD([[subQ4,-1.0]])],"derivedFrom":subQ0}),1.0]])]});}
            var Q19;
            {var subQ0=sQuery(id+"F9.wireOp",EDGE,"E101.MirrorCS");var subQ3=sQuery(id+"F9.wireOp",EDGE,"E73.MirrorCS");var subQ4=makeQuery(id+"F9.imprint","INTERSECT",VERTEX,{"derivedFrom":[subQ3,subQ0]});Q19=makeQuery(id+"F9.imprint","IMPRINT",FACE,{"disambiguationData":[TD([[makeQuery(id+"F9.imprint","IMPRINT",EDGE,{"disambiguationData":[TD([[subQ4,1.0]])],"derivedFrom":subQ0}),1.0]])]});}
            var Q20;
            {var subQ5=sQuery(id+"F9.wireOp",EDGE,"E68.MirrorCS");Q20=makeQuery(id+"F9.imprint","IMPRINT",FACE,{"disambiguationData":[TD([[makeQuery(id+"F9.imprint","IMPRINT",EDGE,{"derivedFrom":subQ5}),-1.0]])]});}
            var Q21;
            {var subQ1=sQuery(id+"F9.wireOp",EDGE,"E75.MirrorCS");var subQ7=sQuery(id+"F9.wireOp",EDGE,"E80.MirrorCS");var subQ8=makeQuery(id+"F9.imprint","INTERSECT",VERTEX,{"derivedFrom":[subQ1,subQ7]});Q21=makeQuery(id+"F9.imprint","IMPRINT",FACE,{"disambiguationData":[TD([[makeQuery(id+"F9.imprint","IMPRINT",EDGE,{"disambiguationData":[TD([[subQ8,-1.0]])],"derivedFrom":subQ1}),1.0]])]});}
            var Q22;
            {var subQ0=sQuery(id+"F9.wireOp",EDGE,"E80.MirrorCS");var subQ3=sQuery(id+"F9.wireOp",EDGE,"E77.MirrorCS");var subQ4=makeQuery(id+"F9.imprint","INTERSECT",VERTEX,{"derivedFrom":[subQ3,subQ0]});Q22=makeQuery(id+"F9.imprint","IMPRINT",FACE,{"disambiguationData":[TD([[makeQuery(id+"F9.imprint","IMPRINT",EDGE,{"disambiguationData":[TD([[subQ4,-1.0]])],"derivedFrom":subQ0}),-1.0]])]});}
            var Q23;
            {var subQ0=sQuery(id+"F9.wireOp",EDGE,"E80.MirrorCS");var subQ3=sQuery(id+"F9.wireOp",EDGE,"E78.MirrorCS");var subQ4=makeQuery(id+"F9.imprint","INTERSECT",VERTEX,{"derivedFrom":[subQ3,subQ0]});Q23=makeQuery(id+"F9.imprint","IMPRINT",FACE,{"disambiguationData":[TD([[makeQuery(id+"F9.imprint","IMPRINT",EDGE,{"disambiguationData":[TD([[subQ4,1.0]])],"derivedFrom":subQ0}),-1.0]])]});}
            var Q24;
            {var subQ3=sQuery(id+"F9.wireOp",EDGE,"E75.MirrorCS");var subQ5=sQuery(id+"F9.wireOp",EDGE,"E80.MirrorCS");var subQ6=makeQuery(id+"F9.imprint","INTERSECT",VERTEX,{"derivedFrom":[subQ3,subQ5]});Q24=makeQuery(id+"F9.imprint","IMPRINT",FACE,{"disambiguationData":[TD([[makeQuery(id+"F9.imprint","IMPRINT",EDGE,{"disambiguationData":[TD([[subQ6,-1.0]])],"derivedFrom":subQ3}),-1.0]])]});}
            var Q25;
            {var subQ5=sQuery(id+"F9.wireOp",EDGE,"E74.MirrorCS");Q25=makeQuery(id+"F9.imprint","IMPRINT",FACE,{"disambiguationData":[TD([[makeQuery(id+"F9.imprint","IMPRINT",EDGE,{"derivedFrom":subQ5}),-1.0]])]});}
            var Q26;
            {var subQ4=sQuery(id+"F9.wireOp",EDGE,"E74.MirrorCS");Q26=makeQuery(id+"F9.imprint","IMPRINT",FACE,{"disambiguationData":[TD([[makeQuery(id+"F9.imprint","IMPRINT",EDGE,{"derivedFrom":subQ4}),1.0]])]});}
            var Q27;
            {var subQ0=sQuery(id+"F9.wireOp",EDGE,"E105");Q27=makeQuery(id+"F9.imprint","IMPRINT",FACE,{"disambiguationData":[TD([[makeQuery(id+"F9.imprint","IMPRINT",EDGE,{"derivedFrom":subQ0}),1.0]])]});}
            var Q28;
            {var subQ3=sQuery(id+"F9.wireOp",EDGE,"E65.MirrorCS");Q28=makeQuery(id+"F9.imprint","IMPRINT",FACE,{"disambiguationData":[TD([[makeQuery(id+"F9.imprint","IMPRINT",EDGE,{"derivedFrom":subQ3}),-1.0]])]});}
            var Q29;
            {var subQ0=sQuery(id+"F9.wireOp",EDGE,"E95.MirrorC");var subQ1=sQuery(id+"F9.wireOp",EDGE,"E86.MirrorCS");var subQ2=makeQuery(id+"F9.imprint","INTERSECT",VERTEX,{"disambiguationData":[OD(1.0)],"derivedFrom":[subQ1,subQ0]});Q29=makeQuery(id+"F9.imprint","IMPRINT",FACE,{"disambiguationData":[TD([[makeQuery(id+"F9.imprint","IMPRINT",EDGE,{"disambiguationData":[TD([[subQ2,-1.0]])],"derivedFrom":subQ1}),-1.0]])]});}
            var Q30;
            {var subQ0=sQuery(id+"F9.wireOp",EDGE,"E92.MirrorCS");var subQ3=sQuery(id+"F9.wireOp",EDGE,"E79.MirrorCS");var subQ4=makeQuery(id+"F9.imprint","INTERSECT",VERTEX,{"derivedFrom":[subQ3,subQ0]});Q30=makeQuery(id+"F9.imprint","IMPRINT",FACE,{"disambiguationData":[TD([[makeQuery(id+"F9.imprint","IMPRINT",EDGE,{"disambiguationData":[TD([[subQ4,-1.0]])],"derivedFrom":subQ0}),-1.0]])]});}
            var Q31;
            {var subQ0=sQuery(id+"F9.wireOp",EDGE,"E95.MirrorC");var subQ3=sQuery(id+"F9.wireOp",EDGE,"E86.MirrorCS");var subQ4=makeQuery(id+"F9.imprint","INTERSECT",VERTEX,{"disambiguationData":[OD(1.0)],"derivedFrom":[subQ3,subQ0]});Q31=makeQuery(id+"F9.imprint","IMPRINT",FACE,{"disambiguationData":[TD([[makeQuery(id+"F9.imprint","IMPRINT",EDGE,{"disambiguationData":[TD([[subQ4,-1.0]])],"derivedFrom":subQ3}),1.0]])]});}
            var Q32;
            {var subQ0=sQuery(id+"F9.wireOp",EDGE,"E92.MirrorCS");var subQ3=sQuery(id+"F9.wireOp",EDGE,"E83.MirrorCS");var subQ4=makeQuery(id+"F9.imprint","INTERSECT",VERTEX,{"derivedFrom":[subQ3,subQ0]});Q32=makeQuery(id+"F9.imprint","IMPRINT",FACE,{"disambiguationData":[TD([[makeQuery(id+"F9.imprint","IMPRINT",EDGE,{"disambiguationData":[TD([[subQ4,1.0]])],"derivedFrom":subQ0}),-1.0]])]});}
            var Q33;
            {var subQ3=sQuery(id+"F9.wireOp",EDGE,"E81.MirrorCS");Q33=makeQuery(id+"F9.imprint","IMPRINT",FACE,{"disambiguationData":[TD([[makeQuery(id+"F9.imprint","IMPRINT",EDGE,{"derivedFrom":subQ3}),-1.0]])]});}
            var Q34;
            {var subQ4=sQuery(id+"F9.wireOp",EDGE,"E72.MirrorCS");Q34=makeQuery(id+"F9.imprint","IMPRINT",FACE,{"disambiguationData":[TD([[makeQuery(id+"F9.imprint","IMPRINT",EDGE,{"derivedFrom":subQ4}),-1.0]])]});}
            var Q35;
            {var subQ1=sQuery(id+"F9.wireOp",EDGE,"E87.MirrorCS");Q35=makeQuery(id+"F9.imprint","IMPRINT",FACE,{"disambiguationData":[TD([[makeQuery(id+"F9.imprint","IMPRINT",EDGE,{"derivedFrom":subQ1}),-1.0]])]});}
            var Q36;
            {var subQ5=sQuery(id+"F9.wireOp",EDGE,"E88.MirrorCS");Q36=makeQuery(id+"F9.imprint","IMPRINT",FACE,{"disambiguationData":[TD([[makeQuery(id+"F9.imprint","IMPRINT",EDGE,{"derivedFrom":subQ5}),1.0]])]});}
            var Q37;
            {var subQ0=sQuery(id+"F9.wireOp",EDGE,"E100.MirrorCS");var subQ1=sQuery(id+"F9.wireOp",EDGE,"E93.MirrorCS");var subQ2=makeQuery(id+"F9.imprint","INTERSECT",VERTEX,{"derivedFrom":[subQ1,subQ0]});Q37=makeQuery(id+"F9.imprint","IMPRINT",FACE,{"disambiguationData":[TD([[makeQuery(id+"F9.imprint","IMPRINT",EDGE,{"disambiguationData":[TD([[subQ2,-1.0]])],"derivedFrom":subQ1}),1.0]])]});}
            var Q38;
            {var subQ0=sQuery(id+"F9.wireOp",EDGE,"E100.MirrorCS");var subQ1=sQuery(id+"F9.wireOp",EDGE,"E93.MirrorCS");var subQ2=makeQuery(id+"F9.imprint","INTERSECT",VERTEX,{"derivedFrom":[subQ1,subQ0]});Q38=makeQuery(id+"F9.imprint","IMPRINT",FACE,{"disambiguationData":[TD([[makeQuery(id+"F9.imprint","IMPRINT",EDGE,{"disambiguationData":[TD([[subQ2,-1.0]])],"derivedFrom":subQ1}),-1.0]])]});}
            var Q39;
            {var subQ0=sQuery(id+"F9.wireOp",EDGE,"E100.MirrorCS");var subQ3=sQuery(id+"F9.wireOp",EDGE,"E89.MirrorCS");var subQ4=makeQuery(id+"F9.imprint","INTERSECT",VERTEX,{"derivedFrom":[subQ3,subQ0]});Q39=makeQuery(id+"F9.imprint","IMPRINT",FACE,{"disambiguationData":[TD([[makeQuery(id+"F9.imprint","IMPRINT",EDGE,{"disambiguationData":[TD([[subQ4,-1.0]])],"derivedFrom":subQ0}),1.0]])]});}
            var Q40;
            {var subQ0=sQuery(id+"F9.wireOp",EDGE,"E100.MirrorCS");var subQ3=sQuery(id+"F9.wireOp",EDGE,"E85.MirrorCS");var subQ4=makeQuery(id+"F9.imprint","INTERSECT",VERTEX,{"derivedFrom":[subQ3,subQ0]});Q40=makeQuery(id+"F9.imprint","IMPRINT",FACE,{"disambiguationData":[TD([[makeQuery(id+"F9.imprint","IMPRINT",EDGE,{"disambiguationData":[TD([[subQ4,1.0]])],"derivedFrom":subQ0}),1.0]])]});}
            var Q41;
            {var subQ5=sQuery(id+"F9.wireOp",EDGE,"E72.MirrorCS");Q41=makeQuery(id+"F9.imprint","IMPRINT",FACE,{"disambiguationData":[TD([[makeQuery(id+"F9.imprint","IMPRINT",EDGE,{"derivedFrom":subQ5}),1.0]])]});}
            extrude(context, id + "F10", {"entities" : qUnion([Q0, Q1, Q2, Q3, Q4, Q5, Q6, Q7, Q8, Q9, Q10, Q11, Q12, Q13, Q14, Q15, Q16, Q17, Q18, Q19, Q20, Q21, Q22, Q23, Q24, Q25, Q26, Q27, Q28, Q29, Q30, Q31, Q32, Q33, Q34, Q35, Q36, Q37, Q38, Q39, Q40, Q41]), "operationType" : NewBodyOperationType.REMOVE, "depth" : 2.5 * mm});
        }
        {
            var Q0;
            Q0=makeQuery(id+"F3.opExtrude","CAP_EDGE",EDGE,{"disambiguationData":[OSD([sQuery(id+"F0.wireOp",EDGE,"E9.left"),sQuery(id+"F0.wireOp",EDGE,"E25.left")])],"isStart":false});
            var Q1;
            {var subQ0=sQuery(id+"F0.wireOp",EDGE,"E2.right");Q1=makeQuery(id+"F8.boolean.opBoolean","SPLIT",EDGE,{"disambiguationData":[TD([makeQuery(id+"F8.opExtrude","SWEPT_FACE",FACE,{"disambiguationData":[OSD([sQuery(id+"F6.wireOp",EDGE,"E27.top")])]})])],"derivedFrom":makeQuery(id+"F3.opExtrude","CAP_EDGE",EDGE,{"disambiguationData":[OSD([subQ0])],"isStart":false})});}
            var Q2;
            {var subQ0=sQuery(id+"F0.wireOp",EDGE,"E2.bottom");Q2=makeQuery(id+"F3.opExtrude","CAP_EDGE",EDGE,{"disambiguationData":[OSD([subQ0]),TDD([makeQuery(id+"F0.imprint","IMPRINT",EDGE,{"disambiguationData":[TD([[makeQuery(id+"F0.imprint","INTERSECT",VERTEX,{"derivedFrom":[sQuery(id+"F0.wireOp",EDGE,"E2.right"),subQ0]}),1.0]])],"derivedFrom":subQ0})])],"isStart":false});}
            var Q3;
            Q3=makeQuery(id+"F3.opExtrude","CAP_EDGE",EDGE,{"disambiguationData":[OSD([sQuery(id+"F0.wireOp",EDGE,"E9.bottom")])],"isStart":false});
            var Q4;
            {var subQ0=sQuery(id+"F0.wireOp",EDGE,"E2.right");var subQ1=sQuery(id+"F0.wireOp",EDGE,"E2.top");Q4=makeQuery(id+"F8.boolean.opBoolean","SPLIT",EDGE,{"disambiguationData":[TD([makeQuery(id+"F3.opExtrude","SWEPT_FACE",FACE,{"disambiguationData":[OSD([subQ1])]})])],"derivedFrom":makeQuery(id+"F3.opExtrude","CAP_EDGE",EDGE,{"disambiguationData":[OSD([subQ0])],"isStart":false})});}
            var Q5;
            Q5=makeQuery(id+"F3.opExtrude","CAP_EDGE",EDGE,{"disambiguationData":[OSD([sQuery(id+"F0.wireOp",EDGE,"E2.top")])],"isStart":false});
            var Q6;
            Q6=makeQuery(id+"F3.opExtrude","CAP_EDGE",EDGE,{"disambiguationData":[OSD([sQuery(id+"F0.wireOp",EDGE,"E5.left")])],"isStart":false});
            var Q7;
            Q7=makeQuery(id+"F3.opExtrude","CAP_EDGE",EDGE,{"disambiguationData":[OSD([sQuery(id+"F0.wireOp",EDGE,"E5.bottom")])],"isStart":false});
            var Q8;
            Q8=makeQuery(id+"F3.opExtrude","CAP_EDGE",EDGE,{"disambiguationData":[OSD([sQuery(id+"F0.wireOp",EDGE,"E7.bottom")])],"isStart":false});
            var Q9;
            {var subQ0=sQuery(id+"F0.wireOp",EDGE,"E2.left");var subQ1=sQuery(id+"F0.wireOp",EDGE,"E2.top");Q9=makeQuery(id+"F7.boolean.opBoolean","SPLIT",EDGE,{"disambiguationData":[TD([makeQuery(id+"F3.opExtrude","SWEPT_FACE",FACE,{"disambiguationData":[OSD([subQ1])]})])],"derivedFrom":makeQuery(id+"F3.opExtrude","CAP_EDGE",EDGE,{"disambiguationData":[OSD([subQ0])],"isStart":false})});}
            var Q10;
            {var subQ0=sQuery(id+"F0.wireOp",EDGE,"E2.left");Q10=makeQuery(id+"F7.boolean.opBoolean","SPLIT",EDGE,{"disambiguationData":[TD([makeQuery(id+"F7.opExtrude","SWEPT_FACE",FACE,{"disambiguationData":[OSD([sQuery(id+"F5.wireOp",EDGE,"E26.top")])]})])],"derivedFrom":makeQuery(id+"F3.opExtrude","CAP_EDGE",EDGE,{"disambiguationData":[OSD([subQ0])],"isStart":false})});}
            var Q11;
            Q11=makeQuery(id+"F3.opExtrude","CAP_EDGE",EDGE,{"disambiguationData":[OSD([sQuery(id+"F0.wireOp",EDGE,"E8.left"),sQuery(id+"F0.wireOp",EDGE,"E24.left")])],"isStart":false});
            var Q12;
            Q12=makeQuery(id+"F3.opExtrude","CAP_EDGE",EDGE,{"disambiguationData":[OSD([sQuery(id+"F0.wireOp",EDGE,"E8.bottom")])],"isStart":false});
            var Q13;
            {var subQ0=sQuery(id+"F0.wireOp",EDGE,"E2.bottom");Q13=makeQuery(id+"F3.opExtrude","CAP_EDGE",EDGE,{"disambiguationData":[OSD([subQ0]),TDD([makeQuery(id+"F0.imprint","IMPRINT",EDGE,{"disambiguationData":[TD([[makeQuery(id+"F0.imprint","INTERSECT",VERTEX,{"derivedFrom":[sQuery(id+"F0.wireOp",EDGE,"E2.left"),subQ0]}),-1.0]])],"derivedFrom":subQ0})])],"isStart":false});}
            var Q14;
            Q14=makeQuery(id+"F3.opExtrude","CAP_EDGE",EDGE,{"disambiguationData":[OSD([sQuery(id+"F0.wireOp",EDGE,"E7.left")])],"isStart":false});
            chamfer(context, id + "F11", {"entities" : qUnion([Q0, Q1, Q2, Q3, Q4, Q5, Q6, Q7, Q8, Q9, Q10, Q11, Q12, Q13, Q14]), "width" : 1 * mm, "tangentPropagation" : true});
        }
        {
            var Q0;
            Q0=makeQuery(id+"F1.opExtrude","CAP_FACE",FACE,{"disambiguationData":[OSD([sQuery(id+"F0.wireOp",EDGE,"E1.left"),sQuery(id+"F0.wireOp",EDGE,"E1.right"),sQuery(id+"F0.wireOp",EDGE,"E1.top"),sQuery(id+"F0.wireOp",EDGE,"E1.bottom"),sQuery(id+"F0.wireOp",EDGE,"E21.left"),sQuery(id+"F0.wireOp",EDGE,"E21.right"),sQuery(id+"F0.wireOp",EDGE,"E23.bottom")])],"isStart":true});
            var sketch = newSketch(context, id + "F12", { "sketchPlane" : qUnion([Q0])});
            skCircle(sketch, "E106", {"center": v(47, 30) * mm, "radius": 12.5 * mm});
            skCircle(sketch, "E107", {"center": v(47, 30) * mm, "radius": 10 * mm});
            skLineSegment(sketch, "E108", {"start": v(47, 30) * mm, "end": v(59.4, 31.52) * mm});
            skLineSegment(sketch, "E109", {"start": v(47, 30) * mm, "end": v(59.4, 28.48) * mm});
            skLineSegment(sketch, "E110", {"start": v(47, 30) * mm, "end": v(59.5, 30) * mm, "construction": true});
            skLineSegment(sketch, "E111", {"start": v(0, -60) * mm, "end": v(0, 29) * mm, "construction": true});
            skLineSegment(sketch, "E112.MirrorCS", {"start": v(-47, 30) * mm, "end": v(-59.5, 30) * mm, "construction": true});
            skLineSegment(sketch, "E113.MirrorCS", {"start": v(-47, 30) * mm, "end": v(-59.4, 28.48) * mm, "construction": true});
            skLineSegment(sketch, "E114.MirrorCS", {"start": v(-47, 30) * mm, "end": v(-59.4, 31.52) * mm, "construction": true});
            skCircle(sketch, "E115.MirrorC", {"center": v(-47, 30) * mm, "radius": 10 * mm, "construction": true});
            skCircle(sketch, "E116.MirrorC", {"center": v(-47, 30) * mm, "radius": 12.5 * mm});
            skCircle(sketch, "E117.MirrorC", {"center": v(-47, 30) * mm, "radius": 12.5 * mm, "construction": true});
            skCircle(sketch, "E118.MirrorC", {"center": v(-47, 30) * mm, "radius": 10 * mm});
            skLineSegment(sketch, "E119.MirrorCS", {"start": v(-47, 30) * mm, "end": v(-59.4, 28.48) * mm});
            skLineSegment(sketch, "E120.MirrorCS", {"start": v(-47, 30) * mm, "end": v(-59.4, 31.52) * mm});
            skSolve(sketch);
        }
        {
            var Q0;
            {var subQ1=sQuery(id+"F12.wireOp",EDGE,"E107");var subQ5=sQuery(id+"F12.wireOp",EDGE,"9eeaa4dd-a2c2-4145-84b5-b6b7ac6f59d0");var subQ6=makeQuery(id+"F12.imprint","INTERSECT",VERTEX,{"disambiguationData":[OD(0.0)],"derivedFrom":[subQ1,subQ5]});Q0=makeQuery(id+"F12.imprint","IMPRINT",FACE,{"disambiguationData":[TD([[makeQuery(id+"F12.imprint","IMPRINT",EDGE,{"disambiguationData":[TD([[subQ6,1.0]])],"derivedFrom":subQ1}),-1.0]])]});}
            var Q1;
            {var subQ1=sQuery(id+"F12.wireOp",EDGE,"E107");var subQ5=sQuery(id+"F12.wireOp",EDGE,"9eeaa4dd-a2c2-4145-84b5-b6b7ac6f59d0");var subQ6=makeQuery(id+"F12.imprint","INTERSECT",VERTEX,{"disambiguationData":[OD(1.0)],"derivedFrom":[subQ1,subQ5]});Q1=makeQuery(id+"F12.imprint","IMPRINT",FACE,{"disambiguationData":[TD([[makeQuery(id+"F12.imprint","IMPRINT",EDGE,{"disambiguationData":[TD([[subQ6,-1.0]])],"derivedFrom":subQ1}),-1.0]])]});}
            var Q2;
            {var subQ3=sQuery(id+"F12.wireOp",EDGE,"E106");var subQ5=sQuery(id+"F12.wireOp",EDGE,"E109");var subQ6=makeQuery(id+"F12.imprint","INTERSECT",VERTEX,{"derivedFrom":[subQ5,subQ3]});Q2=makeQuery(id+"F12.imprint","IMPRINT",FACE,{"disambiguationData":[TD([[makeQuery(id+"F12.imprint","IMPRINT",EDGE,{"disambiguationData":[TD([[subQ6,1.0]])],"derivedFrom":subQ5}),-1.0]])]});}
            var Q3;
            {var subQ0=sQuery(id+"F12.wireOp",EDGE,"E106");var subQ3=sQuery(id+"F12.wireOp",EDGE,"E108");var subQ4=makeQuery(id+"F12.imprint","INTERSECT",VERTEX,{"derivedFrom":[subQ3,subQ0]});Q3=makeQuery(id+"F12.imprint","IMPRINT",FACE,{"disambiguationData":[TD([[makeQuery(id+"F12.imprint","IMPRINT",EDGE,{"disambiguationData":[TD([[subQ4,1.0]])],"derivedFrom":subQ3}),1.0]])]});}
            var Q4;
            {var subQ3=sQuery(id+"F12.wireOp",EDGE,"E116.MirrorC");var subQ5=sQuery(id+"F12.wireOp",EDGE,"E120.MirrorCS");var subQ7=makeQuery(id+"F12.imprint","INTERSECT",VERTEX,{"derivedFrom":[subQ3,subQ5]});Q4=makeQuery(id+"F12.imprint","IMPRINT",FACE,{"disambiguationData":[TD([[makeQuery(id+"F12.imprint","IMPRINT",EDGE,{"disambiguationData":[TD([[subQ7,1.0]])],"derivedFrom":subQ3}),1.0]])]});}
            var Q5;
            {var subQ3=sQuery(id+"F12.wireOp",EDGE,"E116.MirrorC");var subQ5=sQuery(id+"F12.wireOp",EDGE,"E119.MirrorCS");var subQ7=makeQuery(id+"F12.imprint","INTERSECT",VERTEX,{"derivedFrom":[subQ3,subQ5]});Q5=makeQuery(id+"F12.imprint","IMPRINT",FACE,{"disambiguationData":[TD([[makeQuery(id+"F12.imprint","IMPRINT",EDGE,{"disambiguationData":[TD([[subQ7,-1.0]])],"derivedFrom":subQ3}),1.0]])]});}
            extrude(context, id + "F13", {"entities" : qUnion([Q0, Q1, Q2, Q3, Q4, Q5]), "operationType" : NewBodyOperationType.ADD, "oppositeDirection" : true, "depth" : 8 * mm});
        }
        {
            var Q0;
            {var subQ0=sQuery(id+"F0.wireOp",EDGE,"E1.right");var subQ1=sQuery(id+"F12.wireOp",EDGE,"E107");Q0=makeQuery(id+"F13.opExtrude","SWEPT_EDGE",EDGE,{"disambiguationData":[OSD([subQ0,subQ1]),TDD([makeQuery(id+"F12.imprint","INTERSECT",VERTEX,{"disambiguationData":[OD(0.0)],"derivedFrom":[makeQuery(id+"F1.opExtrude","CAP_EDGE",EDGE,{"disambiguationData":[OSD([subQ0])],"isStart":true}),subQ1]})])]});}
            var Q1;
            {var subQ0=sQuery(id+"F12.wireOp",EDGE,"E107");Q1=makeQuery(id+"F13.opExtrude","CAP_EDGE",EDGE,{"disambiguationData":[OSD([subQ0]),TDD([makeQuery(id+"F12.imprint","IMPRINT",EDGE,{"disambiguationData":[TD([[makeQuery(id+"F12.imprint","INTERSECT",VERTEX,{"derivedFrom":[subQ0,sQuery(id+"F12.wireOp",EDGE,"E109")]}),1.0]])],"derivedFrom":subQ0})])],"isStart":false});}
            var Q2;
            {var subQ0=sQuery(id+"F12.wireOp",EDGE,"E106");Q2=makeQuery(id+"F13.opExtrude","CAP_EDGE",EDGE,{"disambiguationData":[OSD([subQ0]),TDD([makeQuery(id+"F12.imprint","IMPRINT",EDGE,{"disambiguationData":[TD([[makeQuery(id+"F12.imprint","INTERSECT",VERTEX,{"derivedFrom":[subQ0,sQuery(id+"F12.wireOp",EDGE,"E109")]}),1.0]])],"derivedFrom":subQ0})])],"isStart":false});}
            var Q3;
            {var subQ0=sQuery(id+"F0.wireOp",EDGE,"E1.right");var subQ1=makeQuery(id+"F1.opExtrude","CAP_EDGE",EDGE,{"disambiguationData":[OSD([subQ0])],"isStart":true});Q3=makeQuery(id+"F13.opExtrude","CAP_EDGE",EDGE,{"disambiguationData":[OSD([subQ0]),TDD([makeQuery(id+"F12.imprint","IMPRINT",EDGE,{"disambiguationData":[TD([[makeQuery(id+"F12.imprint","INTERSECT",VERTEX,{"disambiguationData":[OD(1.0)],"derivedFrom":[subQ1,sQuery(id+"F12.wireOp",EDGE,"E106")]}),1.0]])],"derivedFrom":subQ1})])],"isStart":false});}
            var Q4;
            {var subQ0=sQuery(id+"F0.wireOp",EDGE,"E1.right");var subQ1=sQuery(id+"F12.wireOp",EDGE,"E106");Q4=makeQuery(id+"F13.opExtrude","SWEPT_EDGE",EDGE,{"disambiguationData":[OSD([subQ0,subQ1]),TDD([makeQuery(id+"F12.imprint","INTERSECT",VERTEX,{"disambiguationData":[OD(1.0)],"derivedFrom":[makeQuery(id+"F1.opExtrude","CAP_EDGE",EDGE,{"disambiguationData":[OSD([subQ0])],"isStart":true}),subQ1]})])]});}
            var Q5;
            {var subQ0=sQuery(id+"F12.wireOp",EDGE,"E106");Q5=makeQuery(id+"F13.opExtrude","CAP_EDGE",EDGE,{"disambiguationData":[OSD([subQ0]),TDD([makeQuery(id+"F12.imprint","IMPRINT",EDGE,{"disambiguationData":[TD([[makeQuery(id+"F12.imprint","INTERSECT",VERTEX,{"derivedFrom":[subQ0,sQuery(id+"F12.wireOp",EDGE,"E109")]}),1.0]])],"derivedFrom":subQ0})])],"isStart":true});}
            var Q6;
            Q6=makeQuery(id+"F13.opExtrude","SWEPT_EDGE",EDGE,{"disambiguationData":[OSD([sQuery(id+"F12.wireOp",EDGE,"E106"),sQuery(id+"F12.wireOp",EDGE,"E109")])]});
            var Q7;
            Q7=makeQuery(id+"F13.opExtrude","CAP_EDGE",EDGE,{"disambiguationData":[OSD([sQuery(id+"F12.wireOp",EDGE,"E109")])],"isStart":false});
            var Q8;
            Q8=makeQuery(id+"F13.opExtrude","SWEPT_EDGE",EDGE,{"disambiguationData":[OSD([sQuery(id+"F12.wireOp",EDGE,"E107"),sQuery(id+"F12.wireOp",EDGE,"E109")])]});
            var Q9;
            {var subQ0=sQuery(id+"F0.wireOp",EDGE,"E1.right");var subQ1=sQuery(id+"F12.wireOp",EDGE,"E107");Q9=makeQuery(id+"F13.opExtrude","SWEPT_EDGE",EDGE,{"disambiguationData":[OSD([subQ0,subQ1]),TDD([makeQuery(id+"F12.imprint","INTERSECT",VERTEX,{"disambiguationData":[OD(1.0)],"derivedFrom":[makeQuery(id+"F1.opExtrude","CAP_EDGE",EDGE,{"disambiguationData":[OSD([subQ0])],"isStart":true}),subQ1]})])]});}
            var Q10;
            {var subQ0=sQuery(id+"F12.wireOp",EDGE,"E107");Q10=makeQuery(id+"F13.opExtrude","CAP_EDGE",EDGE,{"disambiguationData":[OSD([subQ0]),TDD([makeQuery(id+"F12.imprint","IMPRINT",EDGE,{"disambiguationData":[TD([[makeQuery(id+"F12.imprint","INTERSECT",VERTEX,{"derivedFrom":[subQ0,sQuery(id+"F12.wireOp",EDGE,"E109")]}),1.0]])],"derivedFrom":subQ0})])],"isStart":true});}
            var Q11;
            Q11=makeQuery(id+"F13.opExtrude","SWEPT_EDGE",EDGE,{"disambiguationData":[OSD([sQuery(id+"F12.wireOp",EDGE,"E106"),sQuery(id+"F12.wireOp",EDGE,"E108")])]});
            var Q12;
            {var subQ0=sQuery(id+"F12.wireOp",EDGE,"E106");Q12=makeQuery(id+"F13.opExtrude","CAP_EDGE",EDGE,{"disambiguationData":[OSD([subQ0]),TDD([makeQuery(id+"F12.imprint","IMPRINT",EDGE,{"disambiguationData":[TD([[makeQuery(id+"F12.imprint","INTERSECT",VERTEX,{"derivedFrom":[subQ0,sQuery(id+"F12.wireOp",EDGE,"E108")]}),-1.0]])],"derivedFrom":subQ0})])],"isStart":true});}
            var Q13;
            {var subQ0=sQuery(id+"F12.wireOp",EDGE,"E107");Q13=makeQuery(id+"F13.opExtrude","CAP_EDGE",EDGE,{"disambiguationData":[OSD([subQ0]),TDD([makeQuery(id+"F12.imprint","IMPRINT",EDGE,{"disambiguationData":[TD([[makeQuery(id+"F12.imprint","INTERSECT",VERTEX,{"derivedFrom":[subQ0,sQuery(id+"F12.wireOp",EDGE,"E108")]}),-1.0]])],"derivedFrom":subQ0})])],"isStart":true});}
            var Q14;
            {var subQ0=sQuery(id+"F12.wireOp",EDGE,"E106");Q14=makeQuery(id+"F13.opExtrude","CAP_EDGE",EDGE,{"disambiguationData":[OSD([subQ0]),TDD([makeQuery(id+"F12.imprint","IMPRINT",EDGE,{"disambiguationData":[TD([[makeQuery(id+"F12.imprint","INTERSECT",VERTEX,{"derivedFrom":[subQ0,sQuery(id+"F12.wireOp",EDGE,"E108")]}),-1.0]])],"derivedFrom":subQ0})])],"isStart":false});}
            var Q15;
            {var subQ0=sQuery(id+"F12.wireOp",EDGE,"E107");Q15=makeQuery(id+"F13.opExtrude","CAP_EDGE",EDGE,{"disambiguationData":[OSD([subQ0]),TDD([makeQuery(id+"F12.imprint","IMPRINT",EDGE,{"disambiguationData":[TD([[makeQuery(id+"F12.imprint","INTERSECT",VERTEX,{"derivedFrom":[subQ0,sQuery(id+"F12.wireOp",EDGE,"E108")]}),-1.0]])],"derivedFrom":subQ0})])],"isStart":false});}
            var Q16;
            {var subQ0=sQuery(id+"F0.wireOp",EDGE,"E1.right");var subQ1=makeQuery(id+"F1.opExtrude","CAP_EDGE",EDGE,{"disambiguationData":[OSD([subQ0])],"isStart":true});Q16=makeQuery(id+"F13.opExtrude","CAP_EDGE",EDGE,{"disambiguationData":[OSD([subQ0]),TDD([makeQuery(id+"F12.imprint","IMPRINT",EDGE,{"disambiguationData":[TD([[makeQuery(id+"F12.imprint","INTERSECT",VERTEX,{"disambiguationData":[OD(0.0)],"derivedFrom":[subQ1,sQuery(id+"F12.wireOp",EDGE,"E106")]}),-1.0]])],"derivedFrom":subQ1})])],"isStart":false});}
            var Q17;
            {var subQ0=sQuery(id+"F0.wireOp",EDGE,"E1.right");var subQ1=sQuery(id+"F12.wireOp",EDGE,"E106");Q17=makeQuery(id+"F13.opExtrude","SWEPT_EDGE",EDGE,{"disambiguationData":[OSD([subQ0,subQ1]),TDD([makeQuery(id+"F12.imprint","INTERSECT",VERTEX,{"disambiguationData":[OD(0.0)],"derivedFrom":[makeQuery(id+"F1.opExtrude","CAP_EDGE",EDGE,{"disambiguationData":[OSD([subQ0])],"isStart":true}),subQ1]})])]});}
            var Q18;
            Q18=makeQuery(id+"F13.opExtrude","CAP_EDGE",EDGE,{"disambiguationData":[OSD([sQuery(id+"F12.wireOp",EDGE,"E108")])],"isStart":true});
            var Q19;
            Q19=makeQuery(id+"F13.opExtrude","SWEPT_EDGE",EDGE,{"disambiguationData":[OSD([sQuery(id+"F12.wireOp",EDGE,"E107"),sQuery(id+"F12.wireOp",EDGE,"E108")])]});
            var Q20;
            Q20=makeQuery(id+"F13.opExtrude","CAP_EDGE",EDGE,{"disambiguationData":[OSD([sQuery(id+"F12.wireOp",EDGE,"E109")])],"isStart":true});
            var Q21;
            Q21=makeQuery(id+"F13.opExtrude","CAP_EDGE",EDGE,{"disambiguationData":[OSD([sQuery(id+"F12.wireOp",EDGE,"E108")])],"isStart":false});
            var Q22;
            {var subQ0=sQuery(id+"F12.wireOp",EDGE,"E116.MirrorC");Q22=makeQuery(id+"F13.opExtrude","CAP_EDGE",EDGE,{"disambiguationData":[OSD([subQ0]),TDD([makeQuery(id+"F12.imprint","IMPRINT",EDGE,{"disambiguationData":[TD([[makeQuery(id+"F12.imprint","INTERSECT",VERTEX,{"derivedFrom":[subQ0,sQuery(id+"F12.wireOp",EDGE,"E119.MirrorCS")]}),-1.0]])],"derivedFrom":subQ0})])],"isStart":true});}
            var Q23;
            {var subQ0=sQuery(id+"F12.wireOp",EDGE,"E118.MirrorC");Q23=makeQuery(id+"F13.opExtrude","CAP_EDGE",EDGE,{"disambiguationData":[OSD([subQ0]),TDD([makeQuery(id+"F12.imprint","IMPRINT",EDGE,{"disambiguationData":[TD([[makeQuery(id+"F12.imprint","INTERSECT",VERTEX,{"derivedFrom":[subQ0,sQuery(id+"F12.wireOp",EDGE,"E119.MirrorCS")]}),-1.0]])],"derivedFrom":subQ0})])],"isStart":true});}
            var Q24;
            {var subQ0=sQuery(id+"F12.wireOp",EDGE,"E118.MirrorC");Q24=makeQuery(id+"F13.opExtrude","CAP_EDGE",EDGE,{"disambiguationData":[OSD([subQ0]),TDD([makeQuery(id+"F12.imprint","IMPRINT",EDGE,{"disambiguationData":[TD([[makeQuery(id+"F12.imprint","INTERSECT",VERTEX,{"derivedFrom":[subQ0,sQuery(id+"F12.wireOp",EDGE,"E120.MirrorCS")]}),1.0]])],"derivedFrom":subQ0})])],"isStart":true});}
            var Q25;
            Q25=makeQuery(id+"F13.opExtrude","CAP_EDGE",EDGE,{"disambiguationData":[OSD([sQuery(id+"F12.wireOp",EDGE,"E120.MirrorCS")])],"isStart":true});
            var Q26;
            {var subQ0=sQuery(id+"F12.wireOp",EDGE,"E116.MirrorC");Q26=makeQuery(id+"F13.opExtrude","CAP_EDGE",EDGE,{"disambiguationData":[OSD([subQ0]),TDD([makeQuery(id+"F12.imprint","IMPRINT",EDGE,{"disambiguationData":[TD([[makeQuery(id+"F12.imprint","INTERSECT",VERTEX,{"derivedFrom":[subQ0,sQuery(id+"F12.wireOp",EDGE,"E120.MirrorCS")]}),1.0]])],"derivedFrom":subQ0})])],"isStart":true});}
            var Q27;
            Q27=makeQuery(id+"F13.opExtrude","SWEPT_EDGE",EDGE,{"disambiguationData":[OSD([sQuery(id+"F12.wireOp",EDGE,"E116.MirrorC"),sQuery(id+"F12.wireOp",EDGE,"E120.MirrorCS")])]});
            var Q28;
            Q28=makeQuery(id+"F13.opExtrude","SWEPT_EDGE",EDGE,{"disambiguationData":[OSD([sQuery(id+"F12.wireOp",EDGE,"E118.MirrorC"),sQuery(id+"F12.wireOp",EDGE,"E120.MirrorCS")])]});
            var Q29;
            Q29=makeQuery(id+"F13.opExtrude","SWEPT_EDGE",EDGE,{"disambiguationData":[OSD([sQuery(id+"F12.wireOp",EDGE,"E116.MirrorC"),sQuery(id+"F12.wireOp",EDGE,"E119.MirrorCS")])]});
            var Q30;
            Q30=makeQuery(id+"F13.opExtrude","SWEPT_EDGE",EDGE,{"disambiguationData":[OSD([sQuery(id+"F12.wireOp",EDGE,"E118.MirrorC"),sQuery(id+"F12.wireOp",EDGE,"E119.MirrorCS")])]});
            var Q31;
            Q31=makeQuery(id+"F13.opExtrude","CAP_EDGE",EDGE,{"disambiguationData":[OSD([sQuery(id+"F12.wireOp",EDGE,"E120.MirrorCS")])],"isStart":false});
            var Q32;
            {var subQ0=sQuery(id+"F12.wireOp",EDGE,"E118.MirrorC");Q32=makeQuery(id+"F13.opExtrude","CAP_EDGE",EDGE,{"disambiguationData":[OSD([subQ0]),TDD([makeQuery(id+"F12.imprint","IMPRINT",EDGE,{"disambiguationData":[TD([[makeQuery(id+"F12.imprint","INTERSECT",VERTEX,{"derivedFrom":[subQ0,sQuery(id+"F12.wireOp",EDGE,"E119.MirrorCS")]}),-1.0]])],"derivedFrom":subQ0})])],"isStart":false});}
            var Q33;
            {var subQ0=sQuery(id+"F12.wireOp",EDGE,"E116.MirrorC");Q33=makeQuery(id+"F13.opExtrude","CAP_EDGE",EDGE,{"disambiguationData":[OSD([subQ0]),TDD([makeQuery(id+"F12.imprint","IMPRINT",EDGE,{"disambiguationData":[TD([[makeQuery(id+"F12.imprint","INTERSECT",VERTEX,{"derivedFrom":[subQ0,sQuery(id+"F12.wireOp",EDGE,"E119.MirrorCS")]}),-1.0]])],"derivedFrom":subQ0})])],"isStart":false});}
            var Q34;
            {var subQ0=sQuery(id+"F0.wireOp",EDGE,"E1.left");var subQ1=sQuery(id+"F12.wireOp",EDGE,"E116.MirrorC");Q34=makeQuery(id+"F13.opExtrude","SWEPT_EDGE",EDGE,{"disambiguationData":[OSD([subQ0,subQ1]),TDD([makeQuery(id+"F12.imprint","INTERSECT",VERTEX,{"disambiguationData":[OD(0.0)],"derivedFrom":[makeQuery(id+"F1.opExtrude","CAP_EDGE",EDGE,{"disambiguationData":[OSD([subQ0])],"isStart":true}),subQ1]})])]});}
            var Q35;
            {var subQ0=sQuery(id+"F0.wireOp",EDGE,"E1.left");var subQ1=makeQuery(id+"F1.opExtrude","CAP_EDGE",EDGE,{"disambiguationData":[OSD([subQ0])],"isStart":true});Q35=makeQuery(id+"F13.opExtrude","CAP_EDGE",EDGE,{"disambiguationData":[OSD([subQ0]),TDD([makeQuery(id+"F12.imprint","IMPRINT",EDGE,{"disambiguationData":[TD([[makeQuery(id+"F12.imprint","INTERSECT",VERTEX,{"disambiguationData":[OD(0.0)],"derivedFrom":[subQ1,sQuery(id+"F12.wireOp",EDGE,"E116.MirrorC")]}),1.0]])],"derivedFrom":subQ1})])],"isStart":false});}
            var Q36;
            {var subQ0=sQuery(id+"F12.wireOp",EDGE,"E118.MirrorC");Q36=makeQuery(id+"F13.opExtrude","CAP_EDGE",EDGE,{"disambiguationData":[OSD([subQ0]),TDD([makeQuery(id+"F12.imprint","IMPRINT",EDGE,{"disambiguationData":[TD([[makeQuery(id+"F12.imprint","INTERSECT",VERTEX,{"derivedFrom":[subQ0,sQuery(id+"F12.wireOp",EDGE,"E120.MirrorCS")]}),1.0]])],"derivedFrom":subQ0})])],"isStart":false});}
            var Q37;
            {var subQ0=sQuery(id+"F12.wireOp",EDGE,"E116.MirrorC");Q37=makeQuery(id+"F13.opExtrude","CAP_EDGE",EDGE,{"disambiguationData":[OSD([subQ0]),TDD([makeQuery(id+"F12.imprint","IMPRINT",EDGE,{"disambiguationData":[TD([[makeQuery(id+"F12.imprint","INTERSECT",VERTEX,{"derivedFrom":[subQ0,sQuery(id+"F12.wireOp",EDGE,"E120.MirrorCS")]}),1.0]])],"derivedFrom":subQ0})])],"isStart":false});}
            var Q38;
            {var subQ0=sQuery(id+"F0.wireOp",EDGE,"E1.left");var subQ1=makeQuery(id+"F1.opExtrude","CAP_EDGE",EDGE,{"disambiguationData":[OSD([subQ0])],"isStart":true});Q38=makeQuery(id+"F13.opExtrude","CAP_EDGE",EDGE,{"disambiguationData":[OSD([subQ0]),TDD([makeQuery(id+"F12.imprint","IMPRINT",EDGE,{"disambiguationData":[TD([[makeQuery(id+"F12.imprint","INTERSECT",VERTEX,{"disambiguationData":[OD(1.0)],"derivedFrom":[subQ1,sQuery(id+"F12.wireOp",EDGE,"E116.MirrorC")]}),-1.0]])],"derivedFrom":subQ1})])],"isStart":false});}
            var Q39;
            {var subQ0=sQuery(id+"F0.wireOp",EDGE,"E1.left");var subQ1=sQuery(id+"F12.wireOp",EDGE,"E116.MirrorC");Q39=makeQuery(id+"F13.opExtrude","SWEPT_EDGE",EDGE,{"disambiguationData":[OSD([subQ0,subQ1]),TDD([makeQuery(id+"F12.imprint","INTERSECT",VERTEX,{"disambiguationData":[OD(1.0)],"derivedFrom":[makeQuery(id+"F1.opExtrude","CAP_EDGE",EDGE,{"disambiguationData":[OSD([subQ0])],"isStart":true}),subQ1]})])]});}
            var Q40;
            {var subQ0=sQuery(id+"F12.wireOp",EDGE,"E106");Q40=makeQuery(id+"F13.opExtrude","CAP_EDGE",EDGE,{"disambiguationData":[OSD([subQ0]),TDD([makeQuery(id+"F12.imprint","IMPRINT",EDGE,{"disambiguationData":[TD([[makeQuery(id+"F12.imprint","INTERSECT",VERTEX,{"derivedFrom":[sQuery(id+"F12.wireOp",EDGE,"E109"),subQ0]}),-1.0]])],"derivedFrom":subQ0})])],"isStart":true});}
            var Q41;
            {var subQ0=sQuery(id+"F12.wireOp",EDGE,"E107");Q41=makeQuery(id+"F13.opExtrude","CAP_EDGE",EDGE,{"disambiguationData":[OSD([subQ0]),TDD([makeQuery(id+"F12.imprint","IMPRINT",EDGE,{"disambiguationData":[TD([[makeQuery(id+"F12.imprint","INTERSECT",VERTEX,{"derivedFrom":[sQuery(id+"F12.wireOp",EDGE,"E109"),subQ0]}),-1.0]])],"derivedFrom":subQ0})])],"isStart":true});}
            var Q42;
            {var subQ0=sQuery(id+"F12.wireOp",EDGE,"E106");Q42=makeQuery(id+"F13.opExtrude","CAP_EDGE",EDGE,{"disambiguationData":[OSD([subQ0]),TDD([makeQuery(id+"F12.imprint","IMPRINT",EDGE,{"disambiguationData":[TD([[makeQuery(id+"F12.imprint","INTERSECT",VERTEX,{"derivedFrom":[sQuery(id+"F12.wireOp",EDGE,"E108"),subQ0]}),1.0]])],"derivedFrom":subQ0})])],"isStart":true});}
            var Q43;
            {var subQ0=sQuery(id+"F0.wireOp",EDGE,"E1.right");var subQ1=makeQuery(id+"F1.opExtrude","CAP_EDGE",EDGE,{"disambiguationData":[OSD([subQ0])],"isStart":true});var subQ2=sQuery(id+"F12.wireOp",EDGE,"E107");var subQ7=sQuery(id+"F12.wireOp",EDGE,"E109");Q43=makeQuery(id+"F13.boolean.opBoolean","SPLIT",EDGE,{"disambiguationData":[TD([makeQuery(id+"F13.opExtrude","SWEPT_FACE",FACE,{"disambiguationData":[OSD([subQ2]),TDD([makeQuery(id+"F12.imprint","IMPRINT",EDGE,{"disambiguationData":[TD([[makeQuery(id+"F12.imprint","INTERSECT",VERTEX,{"derivedFrom":[subQ7,subQ2]}),-1.0]])],"derivedFrom":subQ2})])]})])],"derivedFrom":subQ1});}
            var Q44;
            {var subQ0=sQuery(id+"F12.wireOp",EDGE,"E106");Q44=makeQuery(id+"F13.opExtrude","SWEPT_FACE",FACE,{"disambiguationData":[OSD([subQ0]),TDD([makeQuery(id+"F12.imprint","IMPRINT",EDGE,{"disambiguationData":[TD([[makeQuery(id+"F12.imprint","INTERSECT",VERTEX,{"derivedFrom":[sQuery(id+"F12.wireOp",EDGE,"E108"),subQ0]}),1.0]])],"derivedFrom":subQ0})])]});}
            var Q45;
            Q45=makeQuery(id+"F13.opExtrude","SWEPT_EDGE",EDGE,{"disambiguationData":[OSD([sQuery(id+"F12.wireOp",EDGE,"E109"),sQuery(id+"F12.wireOp",EDGE,"E106")])]});
            var Q46;
            {var subQ0=sQuery(id+"F12.wireOp",EDGE,"E107");Q46=makeQuery(id+"F13.opExtrude","CAP_EDGE",EDGE,{"disambiguationData":[OSD([subQ0]),TDD([makeQuery(id+"F12.imprint","IMPRINT",EDGE,{"disambiguationData":[TD([[makeQuery(id+"F12.imprint","INTERSECT",VERTEX,{"derivedFrom":[sQuery(id+"F12.wireOp",EDGE,"E109"),subQ0]}),-1.0]])],"derivedFrom":subQ0})])],"isStart":false});}
            var Q47;
            {var subQ0=sQuery(id+"F12.wireOp",EDGE,"E107");Q47=makeQuery(id+"F13.opExtrude","CAP_EDGE",EDGE,{"disambiguationData":[OSD([subQ0]),TDD([makeQuery(id+"F12.imprint","IMPRINT",EDGE,{"disambiguationData":[TD([[makeQuery(id+"F12.imprint","INTERSECT",VERTEX,{"derivedFrom":[sQuery(id+"F12.wireOp",EDGE,"E108"),subQ0]}),1.0]])],"derivedFrom":subQ0})])],"isStart":false});}
            var Q48;
            Q48=makeQuery(id+"F13.opExtrude","SWEPT_EDGE",EDGE,{"disambiguationData":[OSD([sQuery(id+"F12.wireOp",EDGE,"E108"),sQuery(id+"F12.wireOp",EDGE,"E107")])]});
            var Q49;
            Q49=makeQuery(id+"F13.opExtrude","SWEPT_EDGE",EDGE,{"disambiguationData":[OSD([sQuery(id+"F12.wireOp",EDGE,"E109"),sQuery(id+"F12.wireOp",EDGE,"E107")])]});
            var Q50;
            {var subQ0=sQuery(id+"F12.wireOp",EDGE,"E106");Q50=makeQuery(id+"F13.opExtrude","CAP_EDGE",EDGE,{"disambiguationData":[OSD([subQ0]),TDD([makeQuery(id+"F12.imprint","IMPRINT",EDGE,{"disambiguationData":[TD([[makeQuery(id+"F12.imprint","INTERSECT",VERTEX,{"derivedFrom":[sQuery(id+"F12.wireOp",EDGE,"E109"),subQ0]}),-1.0]])],"derivedFrom":subQ0})])],"isStart":false});}
            var Q51;
            Q51=makeQuery(id+"F13.opExtrude","CAP_EDGE",EDGE,{"disambiguationData":[OSD([sQuery(id+"F12.wireOp",EDGE,"E109")])],"isStart":false});
            var Q52;
            Q52=makeQuery(id+"F13.opExtrude","CAP_EDGE",EDGE,{"disambiguationData":[OSD([sQuery(id+"F12.wireOp",EDGE,"E109")])],"isStart":true});
            var Q53;
            {var subQ0=sQuery(id+"F0.wireOp",EDGE,"E1.left");var subQ1=sQuery(id+"F0.wireOp",EDGE,"E1.right");var subQ2=sQuery(id+"F12.wireOp",EDGE,"E107");var subQ3=sQuery(id+"F12.wireOp",EDGE,"E106");var subQ4=sQuery(id+"F12.wireOp",EDGE,"E116.MirrorC");var subQ5=sQuery(id+"F12.wireOp",EDGE,"E118.MirrorC");Q53=makeQuery(id+"F13.boolean.opBoolean","MERGE",FACE,{"derivedFrom":[makeQuery(id+"F1.opExtrude","CAP_FACE",FACE,{"disambiguationData":[OSD([subQ0,subQ1,sQuery(id+"F0.wireOp",EDGE,"E1.top"),sQuery(id+"F0.wireOp",EDGE,"E1.bottom"),sQuery(id+"F0.wireOp",EDGE,"E21.left"),sQuery(id+"F0.wireOp",EDGE,"E21.right"),sQuery(id+"F0.wireOp",EDGE,"E23.bottom")])],"isStart":true}),makeQuery(id+"F13.opExtrude","CAP_FACE",FACE,{"disambiguationData":[OSD([subQ1,sQuery(id+"F12.wireOp",EDGE,"E108"),subQ2,subQ3])],"isStart":true}),makeQuery(id+"F13.opExtrude","CAP_FACE",FACE,{"disambiguationData":[OSD([subQ1,sQuery(id+"F12.wireOp",EDGE,"E109"),subQ2,subQ3])],"isStart":true}),makeQuery(id+"F13.opExtrude","CAP_FACE",FACE,{"disambiguationData":[OSD([subQ0,subQ4,subQ5,sQuery(id+"F12.wireOp",EDGE,"E119.MirrorCS")])],"isStart":true}),makeQuery(id+"F13.opExtrude","CAP_FACE",FACE,{"disambiguationData":[OSD([subQ0,subQ4,subQ5,sQuery(id+"F12.wireOp",EDGE,"E120.MirrorCS")])],"isStart":true})]});}
            var Q54;
            Q54=makeQuery(id+"F13.opExtrude","CAP_EDGE",EDGE,{"disambiguationData":[OSD([sQuery(id+"F12.wireOp",EDGE,"E108")])],"isStart":true});
            fillet(context, id + "F14", {"entities" : qUnion([Q0, Q1, Q2, Q3, Q4, Q5, Q6, Q7, Q8, Q9, Q10, Q11, Q12, Q13, Q14, Q15, Q16, Q17, Q18, Q19, Q20, Q21, Q22, Q23, Q24, Q25, Q26, Q27, Q28, Q29, Q30, Q31, Q32, Q33, Q34, Q35, Q36, Q37, Q38, Q39, Q40, Q41, Q42, Q43, Q44, Q45, Q46, Q47, Q48, Q49, Q50, Q51, Q52, Q53, Q54]), "radius" : 1 * mm, "tangentPropagation" : true, "allowEdgeOverflow" : false});
        }
        {
            var Q0;
            Q0=makeQuery(id+"F0.imprint","IMPRINT",FACE,{"disambiguationData":[TD([[makeQuery(id+"F0.imprint","IMPRINT",EDGE,{"derivedFrom":sQuery(id+"F0.wireOp",EDGE,"E2.top")}),1.0]])]});
            var Q1;
            Q1=makeQuery(id+"F0.imprint","IMPRINT",FACE,{"disambiguationData":[TD([[makeQuery(id+"F0.imprint","IMPRINT",EDGE,{"derivedFrom":sQuery(id+"F0.wireOp",EDGE,"E5.right")}),-1.0]])]});
            var Q2;
            Q2=makeQuery(id+"F0.imprint","IMPRINT",FACE,{"disambiguationData":[TD([[makeQuery(id+"F0.imprint","IMPRINT",EDGE,{"derivedFrom":sQuery(id+"F0.wireOp",EDGE,"E7.top")}),-1.0]])]});
            var Q3;
            Q3=makeQuery(id+"F0.imprint","IMPRINT",FACE,{"disambiguationData":[TD([[makeQuery(id+"F0.imprint","IMPRINT",EDGE,{"derivedFrom":sQuery(id+"F0.wireOp",EDGE,"E8.top")}),1.0]])]});
            var Q4;
            Q4=makeQuery(id+"F0.imprint","IMPRINT",FACE,{"disambiguationData":[TD([[makeQuery(id+"F0.imprint","IMPRINT",EDGE,{"derivedFrom":sQuery(id+"F0.wireOp",EDGE,"E9.right")}),1.0]])]});
            var Q5;
            {var subQ1=sQuery(id+"F0.wireOp",EDGE,"E9.top");Q5=makeQuery(id+"F0.imprint","IMPRINT",FACE,{"disambiguationData":[TD([[makeQuery(id+"F0.imprint","IMPRINT",EDGE,{"derivedFrom":subQ1}),-1.0]])]});}
            extrude(context, id + "F15", {"entities" : qUnion([Q0, Q1, Q2, Q3, Q4, Q5]), "oppositeDirection" : true, "depth" : 25 * mm});
        }
        {
            var Q0;
            Q0=makeQuery(id+"F0.imprint","IMPRINT",FACE,{"disambiguationData":[TD([[makeQuery(id+"F0.imprint","IMPRINT",EDGE,{"derivedFrom":sQuery(id+"F0.wireOp",EDGE,"E21.top")}),1.0]])]});
            extrude(context, id + "F16", {"entities" : qUnion([Q0]), "oppositeDirection" : true, "depth" : 5 * mm});
        }
        {
            var Q0;
            Q0=makeQuery(id+"F0.imprint","IMPRINT",FACE,{"disambiguationData":[TD([[makeQuery(id+"F0.imprint","IMPRINT",EDGE,{"derivedFrom":sQuery(id+"F0.wireOp",EDGE,"E1.left")}),1.0]])]});
            extrude(context, id + "F17", {"entities" : qUnion([Q0]), "oppositeDirection" : true, "depth" : 27.5 * mm});
        }
    });
